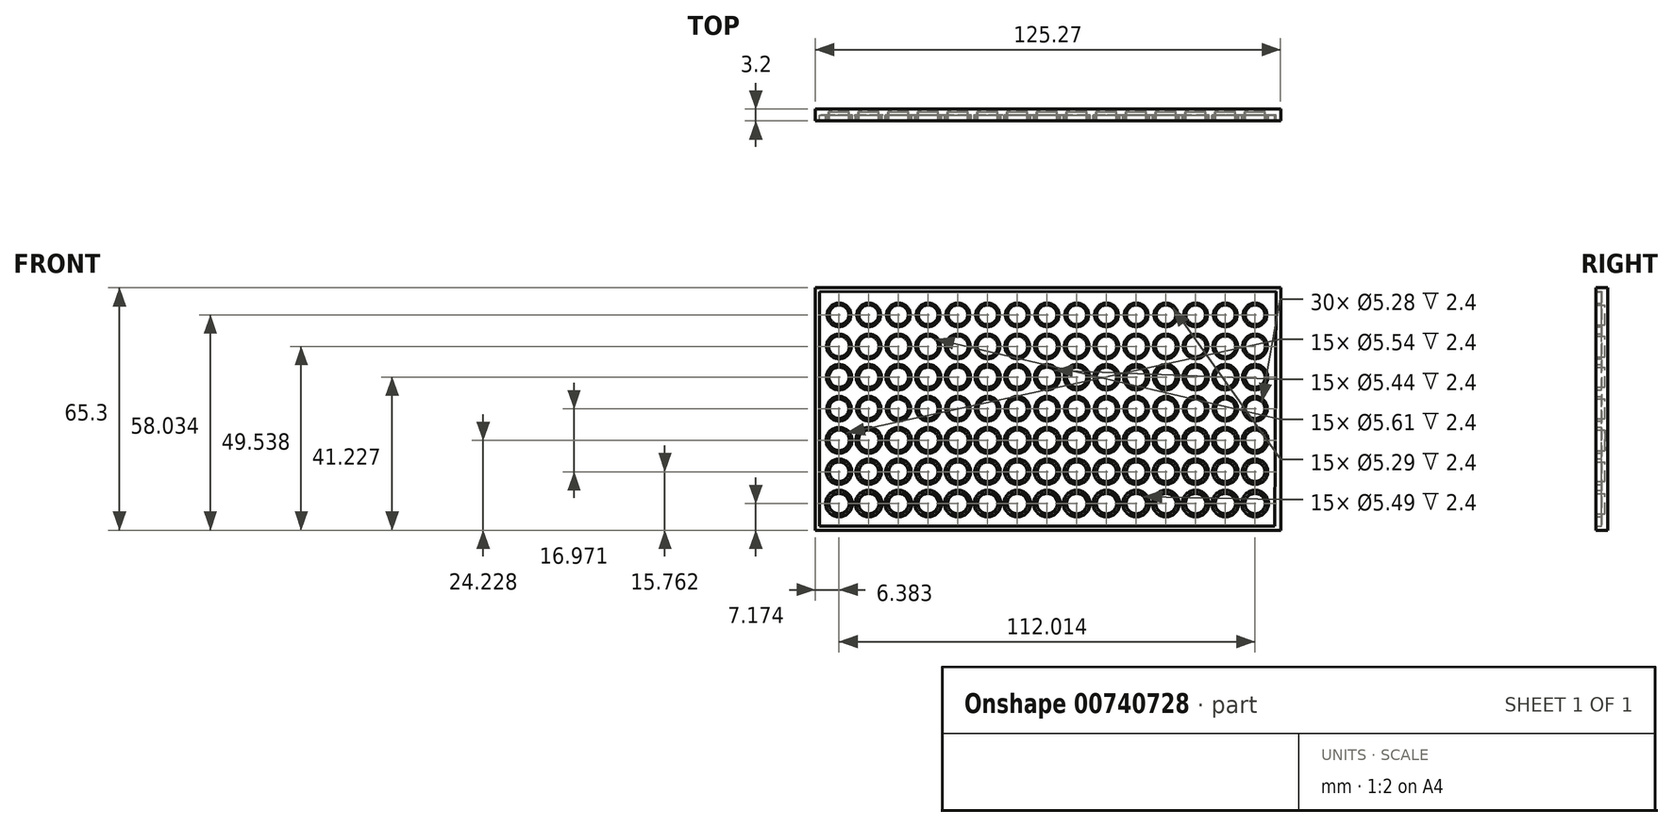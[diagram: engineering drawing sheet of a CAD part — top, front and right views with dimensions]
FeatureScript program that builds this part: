
annotation { "Feature Type Name" : "Feature", "Feature Type Description" : "" }
export const myFeature = defineFeature(function(context is Context, id is Id, definition is map)
    precondition{}
    {
        {
            var Q0;
            Q0=qCreatedBy(makeId("Front.planeOp"),FACE);
            var sketch = newSketch(context, id + "F0", { "sketchPlane" : qUnion([Q0])});
            skLineSegment(sketch, "E0", {"start": v(-62.27, 44.26) * mm, "end": v(-62.27, -21.04) * mm});
            skLineSegment(sketch, "E1", {"start": v(-62.27, -21.04) * mm, "end": v(63, -21.04) * mm});
            skLineSegment(sketch, "E2", {"start": v(63, -21.04) * mm, "end": v(63, 44.26) * mm});
            skLineSegment(sketch, "E3", {"start": v(63, 44.26) * mm, "end": v(-62.27, 44.26) * mm});
            skLineSegment(sketch, "E4", {"start": v(-61.12, 43.24) * mm, "end": v(-61.12, -19.95) * mm});
            skLineSegment(sketch, "E5", {"start": v(-61.12, -19.95) * mm, "end": v(61.46, -19.95) * mm});
            skLineSegment(sketch, "E6", {"start": v(61.46, -19.95) * mm, "end": v(61.83, 43.36) * mm});
            skLineSegment(sketch, "E7", {"start": v(61.83, 43.36) * mm, "end": v(-61.12, 43.24) * mm});
            skCircle(sketch, "E8", {"center": v(-55.89, 28.5) * mm, "radius": 2.8 * mm});
            skCircle(sketch, "E9", {"center": v(-55.89, 28.5) * mm, "radius": 3.32 * mm});
            skCircle(sketch, "E10.1.0.0", {"center": v(-47.89, 28.5) * mm, "radius": 3.32 * mm});
            skCircle(sketch, "E10.1.0.1", {"center": v(-47.89, 28.5) * mm, "radius": 2.8 * mm});
            skCircle(sketch, "E10.2.0.0", {"center": v(-39.89, 28.5) * mm, "radius": 3.32 * mm});
            skCircle(sketch, "E10.2.0.1", {"center": v(-39.89, 28.5) * mm, "radius": 2.8 * mm});
            skCircle(sketch, "E10.3.0.0", {"center": v(-31.88, 28.5) * mm, "radius": 3.32 * mm});
            skCircle(sketch, "E10.3.0.1", {"center": v(-31.88, 28.5) * mm, "radius": 2.8 * mm});
            skCircle(sketch, "E10.4.0.0", {"center": v(-23.88, 28.5) * mm, "radius": 3.32 * mm});
            skCircle(sketch, "E10.4.0.1", {"center": v(-23.88, 28.5) * mm, "radius": 2.8 * mm});
            skCircle(sketch, "E10.5.0.0", {"center": v(-15.88, 28.5) * mm, "radius": 3.32 * mm});
            skCircle(sketch, "E10.5.0.1", {"center": v(-15.88, 28.5) * mm, "radius": 2.8 * mm});
            skCircle(sketch, "E10.6.0.0", {"center": v(-7.88, 28.5) * mm, "radius": 3.32 * mm});
            skCircle(sketch, "E10.6.0.1", {"center": v(-7.88, 28.5) * mm, "radius": 2.8 * mm});
            skCircle(sketch, "E10.7.0.0", {"center": v(0.12, 28.5) * mm, "radius": 3.32 * mm});
            skCircle(sketch, "E10.7.0.1", {"center": v(0.12, 28.5) * mm, "radius": 2.8 * mm});
            skCircle(sketch, "E10.8.0.0", {"center": v(8.12, 28.5) * mm, "radius": 3.32 * mm});
            skCircle(sketch, "E10.8.0.1", {"center": v(8.12, 28.5) * mm, "radius": 2.8 * mm});
            skCircle(sketch, "E10.9.0.0", {"center": v(16.12, 28.5) * mm, "radius": 3.32 * mm});
            skCircle(sketch, "E10.9.0.1", {"center": v(16.12, 28.5) * mm, "radius": 2.8 * mm});
            skCircle(sketch, "E10.10.0.0", {"center": v(24.12, 28.5) * mm, "radius": 3.32 * mm});
            skCircle(sketch, "E10.10.0.1", {"center": v(24.12, 28.5) * mm, "radius": 2.8 * mm});
            skCircle(sketch, "E10.11.0.0", {"center": v(32.12, 28.5) * mm, "radius": 3.32 * mm});
            skCircle(sketch, "E10.11.0.1", {"center": v(32.12, 28.5) * mm, "radius": 2.8 * mm});
            skCircle(sketch, "E10.12.0.0", {"center": v(40.12, 28.5) * mm, "radius": 3.32 * mm});
            skCircle(sketch, "E10.12.0.1", {"center": v(40.12, 28.5) * mm, "radius": 2.8 * mm});
            skCircle(sketch, "E10.13.0.0", {"center": v(48.13, 28.5) * mm, "radius": 3.32 * mm});
            skCircle(sketch, "E10.13.0.1", {"center": v(48.13, 28.5) * mm, "radius": 2.8 * mm});
            skCircle(sketch, "E10.14.0.0", {"center": v(56.13, 28.5) * mm, "radius": 3.32 * mm});
            skCircle(sketch, "E10.14.0.1", {"center": v(56.13, 28.5) * mm, "radius": 2.8 * mm});
            skLineSegment(sketch, "E10.direction1", {"start": v(-55.89, 28.5) * mm, "end": v(-47.89, 28.5) * mm, "construction": true});
            skCircle(sketch, "E11", {"center": v(-55.89, 37) * mm, "radius": 2.65 * mm});
            skCircle(sketch, "E12", {"center": v(-55.89, 37) * mm, "radius": 3.2 * mm});
            skCircle(sketch, "E13.1.0.0", {"center": v(-47.89, 37) * mm, "radius": 3.2 * mm});
            skCircle(sketch, "E13.1.0.1", {"center": v(-47.89, 37) * mm, "radius": 2.65 * mm});
            skCircle(sketch, "E13.2.0.0", {"center": v(-39.89, 37) * mm, "radius": 3.2 * mm});
            skCircle(sketch, "E13.2.0.1", {"center": v(-39.89, 37) * mm, "radius": 2.65 * mm});
            skCircle(sketch, "E13.3.0.0", {"center": v(-31.88, 37) * mm, "radius": 3.2 * mm});
            skCircle(sketch, "E13.3.0.1", {"center": v(-31.88, 37) * mm, "radius": 2.65 * mm});
            skCircle(sketch, "E13.4.0.0", {"center": v(-23.88, 37) * mm, "radius": 3.2 * mm});
            skCircle(sketch, "E13.4.0.1", {"center": v(-23.88, 37) * mm, "radius": 2.65 * mm});
            skCircle(sketch, "E13.5.0.0", {"center": v(-15.88, 37) * mm, "radius": 3.2 * mm});
            skCircle(sketch, "E13.5.0.1", {"center": v(-15.88, 37) * mm, "radius": 2.65 * mm});
            skCircle(sketch, "E13.6.0.0", {"center": v(-7.88, 37) * mm, "radius": 3.2 * mm});
            skCircle(sketch, "E13.6.0.1", {"center": v(-7.88, 37) * mm, "radius": 2.65 * mm});
            skCircle(sketch, "E13.7.0.0", {"center": v(0.12, 37) * mm, "radius": 3.2 * mm});
            skCircle(sketch, "E13.7.0.1", {"center": v(0.12, 37) * mm, "radius": 2.65 * mm});
            skCircle(sketch, "E13.8.0.0", {"center": v(8.12, 37) * mm, "radius": 3.2 * mm});
            skCircle(sketch, "E13.8.0.1", {"center": v(8.12, 37) * mm, "radius": 2.65 * mm});
            skCircle(sketch, "E13.9.0.0", {"center": v(16.12, 37) * mm, "radius": 3.2 * mm});
            skCircle(sketch, "E13.9.0.1", {"center": v(16.12, 37) * mm, "radius": 2.65 * mm});
            skCircle(sketch, "E13.10.0.0", {"center": v(24.12, 37) * mm, "radius": 3.2 * mm});
            skCircle(sketch, "E13.10.0.1", {"center": v(24.12, 37) * mm, "radius": 2.65 * mm});
            skCircle(sketch, "E13.11.0.0", {"center": v(32.12, 37) * mm, "radius": 3.2 * mm});
            skCircle(sketch, "E13.11.0.1", {"center": v(32.12, 37) * mm, "radius": 2.65 * mm});
            skCircle(sketch, "E13.12.0.0", {"center": v(40.12, 37) * mm, "radius": 3.2 * mm});
            skCircle(sketch, "E13.12.0.1", {"center": v(40.12, 37) * mm, "radius": 2.65 * mm});
            skCircle(sketch, "E13.13.0.0", {"center": v(48.13, 37) * mm, "radius": 3.2 * mm});
            skCircle(sketch, "E13.13.0.1", {"center": v(48.13, 37) * mm, "radius": 2.65 * mm});
            skCircle(sketch, "E13.14.0.0", {"center": v(56.13, 37) * mm, "radius": 3.2 * mm});
            skCircle(sketch, "E13.14.0.1", {"center": v(56.13, 37) * mm, "radius": 2.65 * mm});
            skLineSegment(sketch, "E13.direction1", {"start": v(-55.89, 37) * mm, "end": v(-47.89, 37) * mm, "construction": true});
            skCircle(sketch, "E14", {"center": v(-55.89, 20.19) * mm, "radius": 2.72 * mm});
            skCircle(sketch, "E15", {"center": v(-55.89, 20.19) * mm, "radius": 3.4 * mm});
            skCircle(sketch, "E16.1.0.0", {"center": v(-47.89, 20.19) * mm, "radius": 2.72 * mm});
            skCircle(sketch, "E16.1.0.1", {"center": v(-47.89, 20.19) * mm, "radius": 3.4 * mm});
            skCircle(sketch, "E16.2.0.0", {"center": v(-39.89, 20.19) * mm, "radius": 2.72 * mm});
            skCircle(sketch, "E16.2.0.1", {"center": v(-39.89, 20.19) * mm, "radius": 3.4 * mm});
            skCircle(sketch, "E16.3.0.0", {"center": v(-31.88, 20.19) * mm, "radius": 2.72 * mm});
            skCircle(sketch, "E16.3.0.1", {"center": v(-31.88, 20.19) * mm, "radius": 3.4 * mm});
            skCircle(sketch, "E16.4.0.0", {"center": v(-23.88, 20.19) * mm, "radius": 2.72 * mm});
            skCircle(sketch, "E16.4.0.1", {"center": v(-23.88, 20.19) * mm, "radius": 3.4 * mm});
            skCircle(sketch, "E16.5.0.0", {"center": v(-15.88, 20.19) * mm, "radius": 2.72 * mm});
            skCircle(sketch, "E16.5.0.1", {"center": v(-15.88, 20.19) * mm, "radius": 3.4 * mm});
            skCircle(sketch, "E16.6.0.0", {"center": v(-7.88, 20.19) * mm, "radius": 2.72 * mm});
            skCircle(sketch, "E16.6.0.1", {"center": v(-7.88, 20.19) * mm, "radius": 3.4 * mm});
            skCircle(sketch, "E16.7.0.0", {"center": v(0.12, 20.19) * mm, "radius": 2.72 * mm});
            skCircle(sketch, "E16.7.0.1", {"center": v(0.12, 20.19) * mm, "radius": 3.4 * mm});
            skCircle(sketch, "E16.8.0.0", {"center": v(8.12, 20.19) * mm, "radius": 2.72 * mm});
            skCircle(sketch, "E16.8.0.1", {"center": v(8.12, 20.19) * mm, "radius": 3.4 * mm});
            skCircle(sketch, "E16.9.0.0", {"center": v(16.12, 20.19) * mm, "radius": 2.72 * mm});
            skCircle(sketch, "E16.9.0.1", {"center": v(16.12, 20.19) * mm, "radius": 3.4 * mm});
            skCircle(sketch, "E16.10.0.0", {"center": v(24.12, 20.19) * mm, "radius": 2.72 * mm});
            skCircle(sketch, "E16.10.0.1", {"center": v(24.12, 20.19) * mm, "radius": 3.4 * mm});
            skCircle(sketch, "E16.11.0.0", {"center": v(32.12, 20.19) * mm, "radius": 2.72 * mm});
            skCircle(sketch, "E16.11.0.1", {"center": v(32.12, 20.19) * mm, "radius": 3.4 * mm});
            skCircle(sketch, "E16.12.0.0", {"center": v(40.12, 20.19) * mm, "radius": 2.72 * mm});
            skCircle(sketch, "E16.12.0.1", {"center": v(40.12, 20.19) * mm, "radius": 3.4 * mm});
            skCircle(sketch, "E16.13.0.0", {"center": v(48.13, 20.19) * mm, "radius": 2.72 * mm});
            skCircle(sketch, "E16.13.0.1", {"center": v(48.13, 20.19) * mm, "radius": 3.4 * mm});
            skCircle(sketch, "E16.14.0.0", {"center": v(56.13, 20.19) * mm, "radius": 2.72 * mm});
            skCircle(sketch, "E16.14.0.1", {"center": v(56.13, 20.19) * mm, "radius": 3.4 * mm});
            skLineSegment(sketch, "E16.direction1", {"start": v(-55.89, 20.19) * mm, "end": v(-47.89, 20.19) * mm, "construction": true});
            skCircle(sketch, "E17", {"center": v(-55.89, 11.7) * mm, "radius": 2.64 * mm});
            skCircle(sketch, "E18", {"center": v(-55.89, 11.7) * mm, "radius": 3.3 * mm});
            skCircle(sketch, "E19.1.0.0", {"center": v(-47.89, 11.7) * mm, "radius": 2.64 * mm});
            skCircle(sketch, "E19.1.0.1", {"center": v(-47.89, 11.7) * mm, "radius": 3.3 * mm});
            skCircle(sketch, "E19.2.0.0", {"center": v(-39.89, 11.7) * mm, "radius": 2.64 * mm});
            skCircle(sketch, "E19.2.0.1", {"center": v(-39.89, 11.7) * mm, "radius": 3.3 * mm});
            skCircle(sketch, "E19.3.0.0", {"center": v(-31.88, 11.7) * mm, "radius": 2.64 * mm});
            skCircle(sketch, "E19.3.0.1", {"center": v(-31.88, 11.7) * mm, "radius": 3.3 * mm});
            skCircle(sketch, "E19.4.0.0", {"center": v(-23.88, 11.7) * mm, "radius": 2.64 * mm});
            skCircle(sketch, "E19.4.0.1", {"center": v(-23.88, 11.7) * mm, "radius": 3.3 * mm});
            skCircle(sketch, "E19.5.0.0", {"center": v(-15.88, 11.7) * mm, "radius": 2.64 * mm});
            skCircle(sketch, "E19.5.0.1", {"center": v(-15.88, 11.7) * mm, "radius": 3.3 * mm});
            skCircle(sketch, "E19.6.0.0", {"center": v(-7.88, 11.7) * mm, "radius": 2.64 * mm});
            skCircle(sketch, "E19.6.0.1", {"center": v(-7.88, 11.7) * mm, "radius": 3.3 * mm});
            skCircle(sketch, "E19.7.0.0", {"center": v(0.12, 11.7) * mm, "radius": 2.64 * mm});
            skCircle(sketch, "E19.7.0.1", {"center": v(0.12, 11.7) * mm, "radius": 3.3 * mm});
            skCircle(sketch, "E19.8.0.0", {"center": v(8.12, 11.7) * mm, "radius": 2.64 * mm});
            skCircle(sketch, "E19.8.0.1", {"center": v(8.12, 11.7) * mm, "radius": 3.3 * mm});
            skCircle(sketch, "E19.9.0.0", {"center": v(16.12, 11.7) * mm, "radius": 2.64 * mm});
            skCircle(sketch, "E19.9.0.1", {"center": v(16.12, 11.7) * mm, "radius": 3.3 * mm});
            skCircle(sketch, "E19.10.0.0", {"center": v(24.12, 11.7) * mm, "radius": 2.64 * mm});
            skCircle(sketch, "E19.10.0.1", {"center": v(24.12, 11.7) * mm, "radius": 3.3 * mm});
            skCircle(sketch, "E19.11.0.0", {"center": v(32.12, 11.7) * mm, "radius": 2.64 * mm});
            skCircle(sketch, "E19.11.0.1", {"center": v(32.12, 11.7) * mm, "radius": 3.3 * mm});
            skCircle(sketch, "E19.12.0.0", {"center": v(40.12, 11.7) * mm, "radius": 2.64 * mm});
            skCircle(sketch, "E19.12.0.1", {"center": v(40.12, 11.7) * mm, "radius": 3.3 * mm});
            skCircle(sketch, "E19.13.0.0", {"center": v(48.13, 11.7) * mm, "radius": 2.64 * mm});
            skCircle(sketch, "E19.13.0.1", {"center": v(48.13, 11.7) * mm, "radius": 3.3 * mm});
            skCircle(sketch, "E19.14.0.0", {"center": v(56.13, 11.7) * mm, "radius": 2.64 * mm});
            skCircle(sketch, "E19.14.0.1", {"center": v(56.13, 11.7) * mm, "radius": 3.3 * mm});
            skLineSegment(sketch, "E19.direction1", {"start": v(-55.89, 11.7) * mm, "end": v(-47.89, 11.7) * mm, "construction": true});
            skCircle(sketch, "E20", {"center": v(-55.89, 3.19) * mm, "radius": 2.77 * mm});
            skCircle(sketch, "E21", {"center": v(-55.89, 3.19) * mm, "radius": 3.48 * mm});
            skCircle(sketch, "E22.1.0.0", {"center": v(-47.89, 3.19) * mm, "radius": 2.77 * mm});
            skCircle(sketch, "E22.1.0.1", {"center": v(-47.89, 3.19) * mm, "radius": 3.48 * mm});
            skCircle(sketch, "E22.2.0.0", {"center": v(-39.89, 3.19) * mm, "radius": 2.77 * mm});
            skCircle(sketch, "E22.2.0.1", {"center": v(-39.89, 3.19) * mm, "radius": 3.48 * mm});
            skCircle(sketch, "E22.3.0.0", {"center": v(-31.88, 3.19) * mm, "radius": 2.77 * mm});
            skCircle(sketch, "E22.3.0.1", {"center": v(-31.88, 3.19) * mm, "radius": 3.48 * mm});
            skCircle(sketch, "E22.4.0.0", {"center": v(-23.88, 3.19) * mm, "radius": 2.77 * mm});
            skCircle(sketch, "E22.4.0.1", {"center": v(-23.88, 3.19) * mm, "radius": 3.48 * mm});
            skCircle(sketch, "E22.5.0.0", {"center": v(-15.88, 3.19) * mm, "radius": 2.77 * mm});
            skCircle(sketch, "E22.5.0.1", {"center": v(-15.88, 3.19) * mm, "radius": 3.48 * mm});
            skCircle(sketch, "E22.6.0.0", {"center": v(-7.88, 3.19) * mm, "radius": 2.77 * mm});
            skCircle(sketch, "E22.6.0.1", {"center": v(-7.88, 3.19) * mm, "radius": 3.48 * mm});
            skCircle(sketch, "E22.7.0.0", {"center": v(0.12, 3.19) * mm, "radius": 2.77 * mm});
            skCircle(sketch, "E22.7.0.1", {"center": v(0.12, 3.19) * mm, "radius": 3.48 * mm});
            skCircle(sketch, "E22.8.0.0", {"center": v(8.12, 3.19) * mm, "radius": 2.77 * mm});
            skCircle(sketch, "E22.8.0.1", {"center": v(8.12, 3.19) * mm, "radius": 3.48 * mm});
            skCircle(sketch, "E22.9.0.0", {"center": v(16.12, 3.19) * mm, "radius": 2.77 * mm});
            skCircle(sketch, "E22.9.0.1", {"center": v(16.12, 3.19) * mm, "radius": 3.48 * mm});
            skCircle(sketch, "E22.10.0.0", {"center": v(24.12, 3.19) * mm, "radius": 2.77 * mm});
            skCircle(sketch, "E22.10.0.1", {"center": v(24.12, 3.19) * mm, "radius": 3.48 * mm});
            skCircle(sketch, "E22.11.0.0", {"center": v(32.12, 3.19) * mm, "radius": 2.77 * mm});
            skCircle(sketch, "E22.11.0.1", {"center": v(32.12, 3.19) * mm, "radius": 3.48 * mm});
            skCircle(sketch, "E22.12.0.0", {"center": v(40.12, 3.19) * mm, "radius": 2.77 * mm});
            skCircle(sketch, "E22.12.0.1", {"center": v(40.12, 3.19) * mm, "radius": 3.48 * mm});
            skCircle(sketch, "E22.13.0.0", {"center": v(48.13, 3.19) * mm, "radius": 2.77 * mm});
            skCircle(sketch, "E22.13.0.1", {"center": v(48.13, 3.19) * mm, "radius": 3.48 * mm});
            skCircle(sketch, "E22.14.0.0", {"center": v(56.13, 3.19) * mm, "radius": 2.77 * mm});
            skCircle(sketch, "E22.14.0.1", {"center": v(56.13, 3.19) * mm, "radius": 3.48 * mm});
            skLineSegment(sketch, "E22.direction1", {"start": v(-55.89, 3.19) * mm, "end": v(-47.89, 3.19) * mm, "construction": true});
            skCircle(sketch, "E23", {"center": v(-55.89, -5.28) * mm, "radius": 2.64 * mm});
            skCircle(sketch, "E24", {"center": v(-55.89, -5.28) * mm, "radius": 3.44 * mm});
            skCircle(sketch, "E25", {"center": v(-55.89, -13.87) * mm, "radius": 2.74 * mm});
            skCircle(sketch, "E26", {"center": v(-55.89, -13.87) * mm, "radius": 3.6 * mm});
            skCircle(sketch, "E27.1.0.0", {"center": v(-47.89, -5.28) * mm, "radius": 2.64 * mm});
            skCircle(sketch, "E27.1.0.1", {"center": v(-47.89, -5.28) * mm, "radius": 3.44 * mm});
            skCircle(sketch, "E27.2.0.0", {"center": v(-39.89, -5.28) * mm, "radius": 2.64 * mm});
            skCircle(sketch, "E27.2.0.1", {"center": v(-39.89, -5.28) * mm, "radius": 3.44 * mm});
            skCircle(sketch, "E27.3.0.0", {"center": v(-31.88, -5.28) * mm, "radius": 2.64 * mm});
            skCircle(sketch, "E27.3.0.1", {"center": v(-31.88, -5.28) * mm, "radius": 3.44 * mm});
            skCircle(sketch, "E27.4.0.0", {"center": v(-23.88, -5.28) * mm, "radius": 2.64 * mm});
            skCircle(sketch, "E27.4.0.1", {"center": v(-23.88, -5.28) * mm, "radius": 3.44 * mm});
            skCircle(sketch, "E27.5.0.0", {"center": v(-15.88, -5.28) * mm, "radius": 2.64 * mm});
            skCircle(sketch, "E27.5.0.1", {"center": v(-15.88, -5.28) * mm, "radius": 3.44 * mm});
            skCircle(sketch, "E27.6.0.0", {"center": v(-7.88, -5.28) * mm, "radius": 2.64 * mm});
            skCircle(sketch, "E27.6.0.1", {"center": v(-7.88, -5.28) * mm, "radius": 3.44 * mm});
            skCircle(sketch, "E27.7.0.0", {"center": v(0.12, -5.28) * mm, "radius": 2.64 * mm});
            skCircle(sketch, "E27.7.0.1", {"center": v(0.12, -5.28) * mm, "radius": 3.44 * mm});
            skCircle(sketch, "E27.8.0.0", {"center": v(8.12, -5.28) * mm, "radius": 2.64 * mm});
            skCircle(sketch, "E27.8.0.1", {"center": v(8.12, -5.28) * mm, "radius": 3.44 * mm});
            skCircle(sketch, "E27.9.0.0", {"center": v(16.12, -5.28) * mm, "radius": 2.64 * mm});
            skCircle(sketch, "E27.9.0.1", {"center": v(16.12, -5.28) * mm, "radius": 3.44 * mm});
            skCircle(sketch, "E27.10.0.0", {"center": v(24.12, -5.28) * mm, "radius": 2.64 * mm});
            skCircle(sketch, "E27.10.0.1", {"center": v(24.12, -5.28) * mm, "radius": 3.44 * mm});
            skCircle(sketch, "E27.11.0.0", {"center": v(32.12, -5.28) * mm, "radius": 2.64 * mm});
            skCircle(sketch, "E27.11.0.1", {"center": v(32.12, -5.28) * mm, "radius": 3.44 * mm});
            skCircle(sketch, "E27.12.0.0", {"center": v(40.12, -5.28) * mm, "radius": 2.64 * mm});
            skCircle(sketch, "E27.12.0.1", {"center": v(40.12, -5.28) * mm, "radius": 3.44 * mm});
            skCircle(sketch, "E27.13.0.0", {"center": v(48.13, -5.28) * mm, "radius": 2.64 * mm});
            skCircle(sketch, "E27.13.0.1", {"center": v(48.13, -5.28) * mm, "radius": 3.44 * mm});
            skCircle(sketch, "E27.14.0.0", {"center": v(56.13, -5.28) * mm, "radius": 2.64 * mm});
            skCircle(sketch, "E27.14.0.1", {"center": v(56.13, -5.28) * mm, "radius": 3.44 * mm});
            skLineSegment(sketch, "E27.direction1", {"start": v(-55.89, -5.28) * mm, "end": v(-47.89, -5.28) * mm, "construction": true});
            skCircle(sketch, "E28.1.0.0", {"center": v(-47.89, -13.87) * mm, "radius": 2.74 * mm});
            skCircle(sketch, "E28.1.0.1", {"center": v(-47.89, -13.87) * mm, "radius": 3.6 * mm});
            skCircle(sketch, "E28.2.0.0", {"center": v(-39.89, -13.87) * mm, "radius": 2.74 * mm});
            skCircle(sketch, "E28.2.0.1", {"center": v(-39.89, -13.87) * mm, "radius": 3.6 * mm});
            skCircle(sketch, "E28.3.0.0", {"center": v(-31.88, -13.87) * mm, "radius": 2.74 * mm});
            skCircle(sketch, "E28.3.0.1", {"center": v(-31.88, -13.87) * mm, "radius": 3.6 * mm});
            skCircle(sketch, "E28.4.0.0", {"center": v(-23.88, -13.87) * mm, "radius": 2.74 * mm});
            skCircle(sketch, "E28.4.0.1", {"center": v(-23.88, -13.87) * mm, "radius": 3.6 * mm});
            skCircle(sketch, "E28.5.0.0", {"center": v(-15.88, -13.87) * mm, "radius": 2.74 * mm});
            skCircle(sketch, "E28.5.0.1", {"center": v(-15.88, -13.87) * mm, "radius": 3.6 * mm});
            skCircle(sketch, "E28.6.0.0", {"center": v(-7.88, -13.87) * mm, "radius": 2.74 * mm});
            skCircle(sketch, "E28.6.0.1", {"center": v(-7.88, -13.87) * mm, "radius": 3.6 * mm});
            skCircle(sketch, "E28.7.0.0", {"center": v(0.12, -13.87) * mm, "radius": 2.74 * mm});
            skCircle(sketch, "E28.7.0.1", {"center": v(0.12, -13.87) * mm, "radius": 3.6 * mm});
            skCircle(sketch, "E28.8.0.0", {"center": v(8.12, -13.87) * mm, "radius": 2.74 * mm});
            skCircle(sketch, "E28.8.0.1", {"center": v(8.12, -13.87) * mm, "radius": 3.6 * mm});
            skCircle(sketch, "E28.9.0.0", {"center": v(16.12, -13.87) * mm, "radius": 2.74 * mm});
            skCircle(sketch, "E28.9.0.1", {"center": v(16.12, -13.87) * mm, "radius": 3.6 * mm});
            skCircle(sketch, "E28.10.0.0", {"center": v(24.12, -13.87) * mm, "radius": 2.74 * mm});
            skCircle(sketch, "E28.10.0.1", {"center": v(24.12, -13.87) * mm, "radius": 3.6 * mm});
            skCircle(sketch, "E28.11.0.0", {"center": v(32.12, -13.87) * mm, "radius": 2.74 * mm});
            skCircle(sketch, "E28.11.0.1", {"center": v(32.12, -13.87) * mm, "radius": 3.6 * mm});
            skCircle(sketch, "E28.12.0.0", {"center": v(40.12, -13.87) * mm, "radius": 2.74 * mm});
            skCircle(sketch, "E28.12.0.1", {"center": v(40.12, -13.87) * mm, "radius": 3.6 * mm});
            skCircle(sketch, "E28.13.0.0", {"center": v(48.13, -13.87) * mm, "radius": 2.74 * mm});
            skCircle(sketch, "E28.13.0.1", {"center": v(48.13, -13.87) * mm, "radius": 3.6 * mm});
            skCircle(sketch, "E28.14.0.0", {"center": v(56.13, -13.87) * mm, "radius": 2.74 * mm});
            skCircle(sketch, "E28.14.0.1", {"center": v(56.13, -13.87) * mm, "radius": 3.6 * mm});
            skLineSegment(sketch, "E28.direction1", {"start": v(-55.89, -13.87) * mm, "end": v(-47.89, -13.87) * mm, "construction": true});
            skSolve(sketch);
        }
        {
            var Q0;
            Q0=makeQuery(id+"F0.imprint","IMPRINT",FACE,{"disambiguationData":[TD([[makeQuery(id+"F0.imprint","IMPRINT",EDGE,{"derivedFrom":sQuery(id+"F0.wireOp",EDGE,"E0")}),1.0]])]});
            extrude(context, id + "F1", {"entities" : qUnion([Q0]), "depth" : 3.2 * mm, "offsetDistance" : 25.4 * mm});
        }
        {
            var Q0;
            Q0=makeQuery(id+"F0.imprint","IMPRINT",FACE,{"disambiguationData":[TD([[makeQuery(id+"F0.imprint","IMPRINT",EDGE,{"derivedFrom":sQuery(id+"F0.wireOp",EDGE,"E4")}),1.0]])]});
            extrude(context, id + "F2", {"entities" : qUnion([Q0]), "operationType" : NewBodyOperationType.ADD, "depth" : 1.7 * mm, "offsetDistance" : 25.4 * mm});
        }
        {
            var Q0;
            Q0 = qSketchRegion(id + "F0", true);
            var Q1;
            Q1=makeQuery(id+"F0.imprint","IMPRINT",FACE,{"disambiguationData":[TD([[makeQuery(id+"F0.imprint","IMPRINT",EDGE,{"derivedFrom":sQuery(id+"F0.wireOp",EDGE,"E23")}),-1.0]])]});
            var Q2;
            Q2=makeQuery(id+"F0.imprint","IMPRINT",FACE,{"disambiguationData":[TD([[makeQuery(id+"F0.imprint","IMPRINT",EDGE,{"derivedFrom":sQuery(id+"F0.wireOp",EDGE,"E25")}),-1.0]])]});
            var Q3;
            Q3=makeQuery(id+"F0.imprint","IMPRINT",FACE,{"disambiguationData":[TD([[makeQuery(id+"F0.imprint","IMPRINT",EDGE,{"derivedFrom":sQuery(id+"F0.wireOp",EDGE,"E27.1.0.0")}),-1.0]])]});
            var Q4;
            Q4=makeQuery(id+"F0.imprint","IMPRINT",FACE,{"disambiguationData":[TD([[makeQuery(id+"F0.imprint","IMPRINT",EDGE,{"derivedFrom":sQuery(id+"F0.wireOp",EDGE,"E22.1.0.0")}),-1.0]])]});
            var Q5;
            Q5=makeQuery(id+"F0.imprint","IMPRINT",FACE,{"disambiguationData":[TD([[makeQuery(id+"F0.imprint","IMPRINT",EDGE,{"derivedFrom":sQuery(id+"F0.wireOp",EDGE,"E20")}),-1.0]])]});
            var Q6;
            Q6=makeQuery(id+"F0.imprint","IMPRINT",FACE,{"disambiguationData":[TD([[makeQuery(id+"F0.imprint","IMPRINT",EDGE,{"derivedFrom":sQuery(id+"F0.wireOp",EDGE,"E28.1.0.0")}),-1.0]])]});
            var Q7;
            Q7=makeQuery(id+"F0.imprint","IMPRINT",FACE,{"disambiguationData":[TD([[makeQuery(id+"F0.imprint","IMPRINT",EDGE,{"derivedFrom":sQuery(id+"F0.wireOp",EDGE,"E28.2.0.0")}),-1.0]])]});
            var Q8;
            Q8=makeQuery(id+"F0.imprint","IMPRINT",FACE,{"disambiguationData":[TD([[makeQuery(id+"F0.imprint","IMPRINT",EDGE,{"derivedFrom":sQuery(id+"F0.wireOp",EDGE,"E27.2.0.0")}),-1.0]])]});
            var Q9;
            Q9=makeQuery(id+"F0.imprint","IMPRINT",FACE,{"disambiguationData":[TD([[makeQuery(id+"F0.imprint","IMPRINT",EDGE,{"derivedFrom":sQuery(id+"F0.wireOp",EDGE,"E22.2.0.0")}),-1.0]])]});
            var Q10;
            Q10=makeQuery(id+"F0.imprint","IMPRINT",FACE,{"disambiguationData":[TD([[makeQuery(id+"F0.imprint","IMPRINT",EDGE,{"derivedFrom":sQuery(id+"F0.wireOp",EDGE,"E19.2.0.0")}),-1.0]])]});
            var Q11;
            Q11=makeQuery(id+"F0.imprint","IMPRINT",FACE,{"disambiguationData":[TD([[makeQuery(id+"F0.imprint","IMPRINT",EDGE,{"derivedFrom":sQuery(id+"F0.wireOp",EDGE,"E19.1.0.0")}),-1.0]])]});
            var Q12;
            Q12=makeQuery(id+"F0.imprint","IMPRINT",FACE,{"disambiguationData":[TD([[makeQuery(id+"F0.imprint","IMPRINT",EDGE,{"derivedFrom":sQuery(id+"F0.wireOp",EDGE,"E17")}),-1.0]])]});
            var Q13;
            Q13=makeQuery(id+"F0.imprint","IMPRINT",FACE,{"disambiguationData":[TD([[makeQuery(id+"F0.imprint","IMPRINT",EDGE,{"derivedFrom":sQuery(id+"F0.wireOp",EDGE,"E14")}),-1.0]])]});
            var Q14;
            Q14=makeQuery(id+"F0.imprint","IMPRINT",FACE,{"disambiguationData":[TD([[makeQuery(id+"F0.imprint","IMPRINT",EDGE,{"derivedFrom":sQuery(id+"F0.wireOp",EDGE,"E16.1.0.0")}),-1.0]])]});
            var Q15;
            Q15=makeQuery(id+"F0.imprint","IMPRINT",FACE,{"disambiguationData":[TD([[makeQuery(id+"F0.imprint","IMPRINT",EDGE,{"derivedFrom":sQuery(id+"F0.wireOp",EDGE,"E10.1.0.0")}),1.0]])]});
            var Q16;
            Q16=makeQuery(id+"F0.imprint","IMPRINT",FACE,{"disambiguationData":[TD([[makeQuery(id+"F0.imprint","IMPRINT",EDGE,{"derivedFrom":sQuery(id+"F0.wireOp",EDGE,"E8")}),-1.0]])]});
            var Q17;
            Q17=makeQuery(id+"F0.imprint","IMPRINT",FACE,{"disambiguationData":[TD([[makeQuery(id+"F0.imprint","IMPRINT",EDGE,{"derivedFrom":sQuery(id+"F0.wireOp",EDGE,"E16.2.0.0")}),-1.0]])]});
            var Q18;
            Q18=makeQuery(id+"F0.imprint","IMPRINT",FACE,{"disambiguationData":[TD([[makeQuery(id+"F0.imprint","IMPRINT",EDGE,{"derivedFrom":sQuery(id+"F0.wireOp",EDGE,"E10.2.0.0")}),1.0]])]});
            var Q19;
            Q19=makeQuery(id+"F0.imprint","IMPRINT",FACE,{"disambiguationData":[TD([[makeQuery(id+"F0.imprint","IMPRINT",EDGE,{"derivedFrom":sQuery(id+"F0.wireOp",EDGE,"E16.3.0.0")}),-1.0]])]});
            var Q20;
            Q20=makeQuery(id+"F0.imprint","IMPRINT",FACE,{"disambiguationData":[TD([[makeQuery(id+"F0.imprint","IMPRINT",EDGE,{"derivedFrom":sQuery(id+"F0.wireOp",EDGE,"E19.3.0.0")}),-1.0]])]});
            var Q21;
            Q21=makeQuery(id+"F0.imprint","IMPRINT",FACE,{"disambiguationData":[TD([[makeQuery(id+"F0.imprint","IMPRINT",EDGE,{"derivedFrom":sQuery(id+"F0.wireOp",EDGE,"E11")}),-1.0]])]});
            var Q22;
            Q22=makeQuery(id+"F0.imprint","IMPRINT",FACE,{"disambiguationData":[TD([[makeQuery(id+"F0.imprint","IMPRINT",EDGE,{"derivedFrom":sQuery(id+"F0.wireOp",EDGE,"E13.1.0.0")}),1.0]])]});
            var Q23;
            Q23=makeQuery(id+"F0.imprint","IMPRINT",FACE,{"disambiguationData":[TD([[makeQuery(id+"F0.imprint","IMPRINT",EDGE,{"derivedFrom":sQuery(id+"F0.wireOp",EDGE,"E13.2.0.0")}),1.0]])]});
            var Q24;
            Q24=makeQuery(id+"F0.imprint","IMPRINT",FACE,{"disambiguationData":[TD([[makeQuery(id+"F0.imprint","IMPRINT",EDGE,{"derivedFrom":sQuery(id+"F0.wireOp",EDGE,"E10.3.0.0")}),1.0]])]});
            var Q25;
            Q25=makeQuery(id+"F0.imprint","IMPRINT",FACE,{"disambiguationData":[TD([[makeQuery(id+"F0.imprint","IMPRINT",EDGE,{"derivedFrom":sQuery(id+"F0.wireOp",EDGE,"E28.3.0.0")}),-1.0]])]});
            var Q26;
            Q26=makeQuery(id+"F0.imprint","IMPRINT",FACE,{"disambiguationData":[TD([[makeQuery(id+"F0.imprint","IMPRINT",EDGE,{"derivedFrom":sQuery(id+"F0.wireOp",EDGE,"E28.4.0.0")}),-1.0]])]});
            var Q27;
            Q27=makeQuery(id+"F0.imprint","IMPRINT",FACE,{"disambiguationData":[TD([[makeQuery(id+"F0.imprint","IMPRINT",EDGE,{"derivedFrom":sQuery(id+"F0.wireOp",EDGE,"E27.4.0.0")}),-1.0]])]});
            var Q28;
            Q28=makeQuery(id+"F0.imprint","IMPRINT",FACE,{"disambiguationData":[TD([[makeQuery(id+"F0.imprint","IMPRINT",EDGE,{"derivedFrom":sQuery(id+"F0.wireOp",EDGE,"E27.3.0.0")}),-1.0]])]});
            var Q29;
            Q29=makeQuery(id+"F0.imprint","IMPRINT",FACE,{"disambiguationData":[TD([[makeQuery(id+"F0.imprint","IMPRINT",EDGE,{"derivedFrom":sQuery(id+"F0.wireOp",EDGE,"E22.3.0.0")}),-1.0]])]});
            var Q30;
            Q30=makeQuery(id+"F0.imprint","IMPRINT",FACE,{"disambiguationData":[TD([[makeQuery(id+"F0.imprint","IMPRINT",EDGE,{"derivedFrom":sQuery(id+"F0.wireOp",EDGE,"E22.4.0.0")}),-1.0]])]});
            var Q31;
            Q31=makeQuery(id+"F0.imprint","IMPRINT",FACE,{"disambiguationData":[TD([[makeQuery(id+"F0.imprint","IMPRINT",EDGE,{"derivedFrom":sQuery(id+"F0.wireOp",EDGE,"E19.4.0.0")}),-1.0]])]});
            var Q32;
            Q32=makeQuery(id+"F0.imprint","IMPRINT",FACE,{"disambiguationData":[TD([[makeQuery(id+"F0.imprint","IMPRINT",EDGE,{"derivedFrom":sQuery(id+"F0.wireOp",EDGE,"E16.4.0.0")}),-1.0]])]});
            var Q33;
            Q33=makeQuery(id+"F0.imprint","IMPRINT",FACE,{"disambiguationData":[TD([[makeQuery(id+"F0.imprint","IMPRINT",EDGE,{"derivedFrom":sQuery(id+"F0.wireOp",EDGE,"E10.4.0.0")}),1.0]])]});
            var Q34;
            Q34=makeQuery(id+"F0.imprint","IMPRINT",FACE,{"disambiguationData":[TD([[makeQuery(id+"F0.imprint","IMPRINT",EDGE,{"derivedFrom":sQuery(id+"F0.wireOp",EDGE,"E13.4.0.0")}),1.0]])]});
            var Q35;
            Q35=makeQuery(id+"F0.imprint","IMPRINT",FACE,{"disambiguationData":[TD([[makeQuery(id+"F0.imprint","IMPRINT",EDGE,{"derivedFrom":sQuery(id+"F0.wireOp",EDGE,"E13.3.0.0")}),1.0]])]});
            var Q36;
            Q36=makeQuery(id+"F0.imprint","IMPRINT",FACE,{"disambiguationData":[TD([[makeQuery(id+"F0.imprint","IMPRINT",EDGE,{"derivedFrom":sQuery(id+"F0.wireOp",EDGE,"E13.5.0.0")}),1.0]])]});
            var Q37;
            Q37=makeQuery(id+"F0.imprint","IMPRINT",FACE,{"disambiguationData":[TD([[makeQuery(id+"F0.imprint","IMPRINT",EDGE,{"derivedFrom":sQuery(id+"F0.wireOp",EDGE,"E13.6.0.0")}),1.0]])]});
            var Q38;
            Q38=makeQuery(id+"F0.imprint","IMPRINT",FACE,{"disambiguationData":[TD([[makeQuery(id+"F0.imprint","IMPRINT",EDGE,{"derivedFrom":sQuery(id+"F0.wireOp",EDGE,"E13.7.0.0")}),1.0]])]});
            var Q39;
            Q39=makeQuery(id+"F0.imprint","IMPRINT",FACE,{"disambiguationData":[TD([[makeQuery(id+"F0.imprint","IMPRINT",EDGE,{"derivedFrom":sQuery(id+"F0.wireOp",EDGE,"E10.7.0.0")}),1.0]])]});
            var Q40;
            Q40=makeQuery(id+"F0.imprint","IMPRINT",FACE,{"disambiguationData":[TD([[makeQuery(id+"F0.imprint","IMPRINT",EDGE,{"derivedFrom":sQuery(id+"F0.wireOp",EDGE,"E10.6.0.0")}),1.0]])]});
            var Q41;
            Q41=makeQuery(id+"F0.imprint","IMPRINT",FACE,{"disambiguationData":[TD([[makeQuery(id+"F0.imprint","IMPRINT",EDGE,{"derivedFrom":sQuery(id+"F0.wireOp",EDGE,"E10.5.0.0")}),1.0]])]});
            var Q42;
            Q42=makeQuery(id+"F0.imprint","IMPRINT",FACE,{"disambiguationData":[TD([[makeQuery(id+"F0.imprint","IMPRINT",EDGE,{"derivedFrom":sQuery(id+"F0.wireOp",EDGE,"E16.5.0.0")}),-1.0]])]});
            var Q43;
            Q43=makeQuery(id+"F0.imprint","IMPRINT",FACE,{"disambiguationData":[TD([[makeQuery(id+"F0.imprint","IMPRINT",EDGE,{"derivedFrom":sQuery(id+"F0.wireOp",EDGE,"E16.6.0.0")}),-1.0]])]});
            var Q44;
            Q44=makeQuery(id+"F0.imprint","IMPRINT",FACE,{"disambiguationData":[TD([[makeQuery(id+"F0.imprint","IMPRINT",EDGE,{"derivedFrom":sQuery(id+"F0.wireOp",EDGE,"E16.7.0.0")}),-1.0]])]});
            var Q45;
            Q45=makeQuery(id+"F0.imprint","IMPRINT",FACE,{"disambiguationData":[TD([[makeQuery(id+"F0.imprint","IMPRINT",EDGE,{"derivedFrom":sQuery(id+"F0.wireOp",EDGE,"E19.7.0.0")}),-1.0]])]});
            var Q46;
            Q46=makeQuery(id+"F0.imprint","IMPRINT",FACE,{"disambiguationData":[TD([[makeQuery(id+"F0.imprint","IMPRINT",EDGE,{"derivedFrom":sQuery(id+"F0.wireOp",EDGE,"E19.6.0.0")}),-1.0]])]});
            var Q47;
            Q47=makeQuery(id+"F0.imprint","IMPRINT",FACE,{"disambiguationData":[TD([[makeQuery(id+"F0.imprint","IMPRINT",EDGE,{"derivedFrom":sQuery(id+"F0.wireOp",EDGE,"E19.5.0.0")}),-1.0]])]});
            var Q48;
            Q48=makeQuery(id+"F0.imprint","IMPRINT",FACE,{"disambiguationData":[TD([[makeQuery(id+"F0.imprint","IMPRINT",EDGE,{"derivedFrom":sQuery(id+"F0.wireOp",EDGE,"E22.5.0.0")}),-1.0]])]});
            var Q49;
            Q49=makeQuery(id+"F0.imprint","IMPRINT",FACE,{"disambiguationData":[TD([[makeQuery(id+"F0.imprint","IMPRINT",EDGE,{"derivedFrom":sQuery(id+"F0.wireOp",EDGE,"E22.6.0.0")}),-1.0]])]});
            var Q50;
            Q50=makeQuery(id+"F0.imprint","IMPRINT",FACE,{"disambiguationData":[TD([[makeQuery(id+"F0.imprint","IMPRINT",EDGE,{"derivedFrom":sQuery(id+"F0.wireOp",EDGE,"E27.5.0.0")}),-1.0]])]});
            var Q51;
            Q51=makeQuery(id+"F0.imprint","IMPRINT",FACE,{"disambiguationData":[TD([[makeQuery(id+"F0.imprint","IMPRINT",EDGE,{"derivedFrom":sQuery(id+"F0.wireOp",EDGE,"E27.6.0.0")}),-1.0]])]});
            var Q52;
            Q52=makeQuery(id+"F0.imprint","IMPRINT",FACE,{"disambiguationData":[TD([[makeQuery(id+"F0.imprint","IMPRINT",EDGE,{"derivedFrom":sQuery(id+"F0.wireOp",EDGE,"E27.7.0.0")}),-1.0]])]});
            var Q53;
            Q53=makeQuery(id+"F0.imprint","IMPRINT",FACE,{"disambiguationData":[TD([[makeQuery(id+"F0.imprint","IMPRINT",EDGE,{"derivedFrom":sQuery(id+"F0.wireOp",EDGE,"E22.7.0.0")}),-1.0]])]});
            var Q54;
            Q54=makeQuery(id+"F0.imprint","IMPRINT",FACE,{"disambiguationData":[TD([[makeQuery(id+"F0.imprint","IMPRINT",EDGE,{"derivedFrom":sQuery(id+"F0.wireOp",EDGE,"E28.7.0.0")}),-1.0]])]});
            var Q55;
            Q55=makeQuery(id+"F0.imprint","IMPRINT",FACE,{"disambiguationData":[TD([[makeQuery(id+"F0.imprint","IMPRINT",EDGE,{"derivedFrom":sQuery(id+"F0.wireOp",EDGE,"E28.6.0.0")}),-1.0]])]});
            var Q56;
            Q56=makeQuery(id+"F0.imprint","IMPRINT",FACE,{"disambiguationData":[TD([[makeQuery(id+"F0.imprint","IMPRINT",EDGE,{"derivedFrom":sQuery(id+"F0.wireOp",EDGE,"E28.5.0.0")}),-1.0]])]});
            var Q57;
            Q57=makeQuery(id+"F0.imprint","IMPRINT",FACE,{"disambiguationData":[TD([[makeQuery(id+"F0.imprint","IMPRINT",EDGE,{"derivedFrom":sQuery(id+"F0.wireOp",EDGE,"E16.12.0.0")}),-1.0]])]});
            var Q58;
            Q58=makeQuery(id+"F0.imprint","IMPRINT",FACE,{"disambiguationData":[TD([[makeQuery(id+"F0.imprint","IMPRINT",EDGE,{"derivedFrom":sQuery(id+"F0.wireOp",EDGE,"E10.12.0.0")}),1.0]])]});
            var Q59;
            Q59=makeQuery(id+"F0.imprint","IMPRINT",FACE,{"disambiguationData":[TD([[makeQuery(id+"F0.imprint","IMPRINT",EDGE,{"derivedFrom":sQuery(id+"F0.wireOp",EDGE,"E10.11.0.0")}),1.0]])]});
            var Q60;
            Q60=makeQuery(id+"F0.imprint","IMPRINT",FACE,{"disambiguationData":[TD([[makeQuery(id+"F0.imprint","IMPRINT",EDGE,{"derivedFrom":sQuery(id+"F0.wireOp",EDGE,"E10.10.0.0")}),1.0]])]});
            var Q61;
            Q61=makeQuery(id+"F0.imprint","IMPRINT",FACE,{"disambiguationData":[TD([[makeQuery(id+"F0.imprint","IMPRINT",EDGE,{"derivedFrom":sQuery(id+"F0.wireOp",EDGE,"E16.10.0.0")}),-1.0]])]});
            var Q62;
            Q62=makeQuery(id+"F0.imprint","IMPRINT",FACE,{"disambiguationData":[TD([[makeQuery(id+"F0.imprint","IMPRINT",EDGE,{"derivedFrom":sQuery(id+"F0.wireOp",EDGE,"E19.10.0.0")}),-1.0]])]});
            var Q63;
            Q63=makeQuery(id+"F0.imprint","IMPRINT",FACE,{"disambiguationData":[TD([[makeQuery(id+"F0.imprint","IMPRINT",EDGE,{"derivedFrom":sQuery(id+"F0.wireOp",EDGE,"E16.11.0.0")}),-1.0]])]});
            var Q64;
            Q64=makeQuery(id+"F0.imprint","IMPRINT",FACE,{"disambiguationData":[TD([[makeQuery(id+"F0.imprint","IMPRINT",EDGE,{"derivedFrom":sQuery(id+"F0.wireOp",EDGE,"E19.11.0.0")}),-1.0]])]});
            var Q65;
            Q65=makeQuery(id+"F0.imprint","IMPRINT",FACE,{"disambiguationData":[TD([[makeQuery(id+"F0.imprint","IMPRINT",EDGE,{"derivedFrom":sQuery(id+"F0.wireOp",EDGE,"E22.11.0.0")}),-1.0]])]});
            var Q66;
            Q66=makeQuery(id+"F0.imprint","IMPRINT",FACE,{"disambiguationData":[TD([[makeQuery(id+"F0.imprint","IMPRINT",EDGE,{"derivedFrom":sQuery(id+"F0.wireOp",EDGE,"E22.12.0.0")}),-1.0]])]});
            var Q67;
            Q67=makeQuery(id+"F0.imprint","IMPRINT",FACE,{"disambiguationData":[TD([[makeQuery(id+"F0.imprint","IMPRINT",EDGE,{"derivedFrom":sQuery(id+"F0.wireOp",EDGE,"E22.13.0.0")}),-1.0]])]});
            var Q68;
            Q68=makeQuery(id+"F0.imprint","IMPRINT",FACE,{"disambiguationData":[TD([[makeQuery(id+"F0.imprint","IMPRINT",EDGE,{"derivedFrom":sQuery(id+"F0.wireOp",EDGE,"E19.13.0.0")}),-1.0]])]});
            var Q69;
            Q69=makeQuery(id+"F0.imprint","IMPRINT",FACE,{"disambiguationData":[TD([[makeQuery(id+"F0.imprint","IMPRINT",EDGE,{"derivedFrom":sQuery(id+"F0.wireOp",EDGE,"E19.12.0.0")}),-1.0]])]});
            var Q70;
            Q70=makeQuery(id+"F0.imprint","IMPRINT",FACE,{"disambiguationData":[TD([[makeQuery(id+"F0.imprint","IMPRINT",EDGE,{"derivedFrom":sQuery(id+"F0.wireOp",EDGE,"E16.13.0.0")}),-1.0]])]});
            var Q71;
            Q71=makeQuery(id+"F0.imprint","IMPRINT",FACE,{"disambiguationData":[TD([[makeQuery(id+"F0.imprint","IMPRINT",EDGE,{"derivedFrom":sQuery(id+"F0.wireOp",EDGE,"E10.13.0.0")}),1.0]])]});
            var Q72;
            Q72=makeQuery(id+"F0.imprint","IMPRINT",FACE,{"disambiguationData":[TD([[makeQuery(id+"F0.imprint","IMPRINT",EDGE,{"derivedFrom":sQuery(id+"F0.wireOp",EDGE,"E13.13.0.0")}),1.0]])]});
            var Q73;
            Q73=makeQuery(id+"F0.imprint","IMPRINT",FACE,{"disambiguationData":[TD([[makeQuery(id+"F0.imprint","IMPRINT",EDGE,{"derivedFrom":sQuery(id+"F0.wireOp",EDGE,"E13.12.0.0")}),1.0]])]});
            var Q74;
            Q74=makeQuery(id+"F0.imprint","IMPRINT",FACE,{"disambiguationData":[TD([[makeQuery(id+"F0.imprint","IMPRINT",EDGE,{"derivedFrom":sQuery(id+"F0.wireOp",EDGE,"E13.11.0.0")}),1.0]])]});
            var Q75;
            Q75=makeQuery(id+"F0.imprint","IMPRINT",FACE,{"disambiguationData":[TD([[makeQuery(id+"F0.imprint","IMPRINT",EDGE,{"derivedFrom":sQuery(id+"F0.wireOp",EDGE,"E10.14.0.0")}),1.0]])]});
            var Q76;
            Q76=makeQuery(id+"F0.imprint","IMPRINT",FACE,{"disambiguationData":[TD([[makeQuery(id+"F0.imprint","IMPRINT",EDGE,{"derivedFrom":sQuery(id+"F0.wireOp",EDGE,"E22.14.0.0")}),-1.0]])]});
            var Q77;
            Q77=makeQuery(id+"F0.imprint","IMPRINT",FACE,{"disambiguationData":[TD([[makeQuery(id+"F0.imprint","IMPRINT",EDGE,{"derivedFrom":sQuery(id+"F0.wireOp",EDGE,"E27.13.0.0")}),-1.0]])]});
            var Q78;
            Q78=makeQuery(id+"F0.imprint","IMPRINT",FACE,{"disambiguationData":[TD([[makeQuery(id+"F0.imprint","IMPRINT",EDGE,{"derivedFrom":sQuery(id+"F0.wireOp",EDGE,"E13.14.0.0")}),1.0]])]});
            var Q79;
            Q79=makeQuery(id+"F0.imprint","IMPRINT",FACE,{"disambiguationData":[TD([[makeQuery(id+"F0.imprint","IMPRINT",EDGE,{"derivedFrom":sQuery(id+"F0.wireOp",EDGE,"E13.10.0.0")}),1.0]])]});
            var Q80;
            Q80=makeQuery(id+"F0.imprint","IMPRINT",FACE,{"disambiguationData":[TD([[makeQuery(id+"F0.imprint","IMPRINT",EDGE,{"derivedFrom":sQuery(id+"F0.wireOp",EDGE,"E13.9.0.0")}),1.0]])]});
            var Q81;
            Q81=makeQuery(id+"F0.imprint","IMPRINT",FACE,{"disambiguationData":[TD([[makeQuery(id+"F0.imprint","IMPRINT",EDGE,{"derivedFrom":sQuery(id+"F0.wireOp",EDGE,"E13.8.0.0")}),1.0]])]});
            var Q82;
            Q82=makeQuery(id+"F0.imprint","IMPRINT",FACE,{"disambiguationData":[TD([[makeQuery(id+"F0.imprint","IMPRINT",EDGE,{"derivedFrom":sQuery(id+"F0.wireOp",EDGE,"E10.8.0.0")}),1.0]])]});
            var Q83;
            Q83=makeQuery(id+"F0.imprint","IMPRINT",FACE,{"disambiguationData":[TD([[makeQuery(id+"F0.imprint","IMPRINT",EDGE,{"derivedFrom":sQuery(id+"F0.wireOp",EDGE,"E10.9.0.0")}),1.0]])]});
            var Q84;
            Q84=makeQuery(id+"F0.imprint","IMPRINT",FACE,{"disambiguationData":[TD([[makeQuery(id+"F0.imprint","IMPRINT",EDGE,{"derivedFrom":sQuery(id+"F0.wireOp",EDGE,"E22.8.0.0")}),-1.0]])]});
            var Q85;
            Q85=makeQuery(id+"F0.imprint","IMPRINT",FACE,{"disambiguationData":[TD([[makeQuery(id+"F0.imprint","IMPRINT",EDGE,{"derivedFrom":sQuery(id+"F0.wireOp",EDGE,"E22.9.0.0")}),-1.0]])]});
            var Q86;
            Q86=makeQuery(id+"F0.imprint","IMPRINT",FACE,{"disambiguationData":[TD([[makeQuery(id+"F0.imprint","IMPRINT",EDGE,{"derivedFrom":sQuery(id+"F0.wireOp",EDGE,"E19.9.0.0")}),-1.0]])]});
            var Q87;
            Q87=makeQuery(id+"F0.imprint","IMPRINT",FACE,{"disambiguationData":[TD([[makeQuery(id+"F0.imprint","IMPRINT",EDGE,{"derivedFrom":sQuery(id+"F0.wireOp",EDGE,"E16.9.0.0")}),-1.0]])]});
            var Q88;
            Q88=makeQuery(id+"F0.imprint","IMPRINT",FACE,{"disambiguationData":[TD([[makeQuery(id+"F0.imprint","IMPRINT",EDGE,{"derivedFrom":sQuery(id+"F0.wireOp",EDGE,"E16.8.0.0")}),-1.0]])]});
            var Q89;
            Q89=makeQuery(id+"F0.imprint","IMPRINT",FACE,{"disambiguationData":[TD([[makeQuery(id+"F0.imprint","IMPRINT",EDGE,{"derivedFrom":sQuery(id+"F0.wireOp",EDGE,"E19.8.0.0")}),-1.0]])]});
            var Q90;
            Q90=makeQuery(id+"F0.imprint","IMPRINT",FACE,{"disambiguationData":[TD([[makeQuery(id+"F0.imprint","IMPRINT",EDGE,{"derivedFrom":sQuery(id+"F0.wireOp",EDGE,"E22.10.0.0")}),-1.0]])]});
            var Q91;
            Q91=makeQuery(id+"F0.imprint","IMPRINT",FACE,{"disambiguationData":[TD([[makeQuery(id+"F0.imprint","IMPRINT",EDGE,{"derivedFrom":sQuery(id+"F0.wireOp",EDGE,"E28.10.0.0")}),-1.0]])]});
            var Q92;
            Q92=makeQuery(id+"F0.imprint","IMPRINT",FACE,{"disambiguationData":[TD([[makeQuery(id+"F0.imprint","IMPRINT",EDGE,{"derivedFrom":sQuery(id+"F0.wireOp",EDGE,"E28.11.0.0")}),-1.0]])]});
            var Q93;
            Q93=makeQuery(id+"F0.imprint","IMPRINT",FACE,{"disambiguationData":[TD([[makeQuery(id+"F0.imprint","IMPRINT",EDGE,{"derivedFrom":sQuery(id+"F0.wireOp",EDGE,"E27.11.0.0")}),-1.0]])]});
            var Q94;
            Q94=makeQuery(id+"F0.imprint","IMPRINT",FACE,{"disambiguationData":[TD([[makeQuery(id+"F0.imprint","IMPRINT",EDGE,{"derivedFrom":sQuery(id+"F0.wireOp",EDGE,"E27.10.0.0")}),-1.0]])]});
            var Q95;
            Q95=makeQuery(id+"F0.imprint","IMPRINT",FACE,{"disambiguationData":[TD([[makeQuery(id+"F0.imprint","IMPRINT",EDGE,{"derivedFrom":sQuery(id+"F0.wireOp",EDGE,"E27.9.0.0")}),-1.0]])]});
            var Q96;
            Q96=makeQuery(id+"F0.imprint","IMPRINT",FACE,{"disambiguationData":[TD([[makeQuery(id+"F0.imprint","IMPRINT",EDGE,{"derivedFrom":sQuery(id+"F0.wireOp",EDGE,"E27.8.0.0")}),-1.0]])]});
            var Q97;
            Q97=makeQuery(id+"F0.imprint","IMPRINT",FACE,{"disambiguationData":[TD([[makeQuery(id+"F0.imprint","IMPRINT",EDGE,{"derivedFrom":sQuery(id+"F0.wireOp",EDGE,"E28.9.0.0")}),-1.0]])]});
            var Q98;
            Q98=makeQuery(id+"F0.imprint","IMPRINT",FACE,{"disambiguationData":[TD([[makeQuery(id+"F0.imprint","IMPRINT",EDGE,{"derivedFrom":sQuery(id+"F0.wireOp",EDGE,"E28.8.0.0")}),-1.0]])]});
            var Q99;
            Q99=makeQuery(id+"F0.imprint","IMPRINT",FACE,{"disambiguationData":[TD([[makeQuery(id+"F0.imprint","IMPRINT",EDGE,{"derivedFrom":sQuery(id+"F0.wireOp",EDGE,"E28.12.0.0")}),-1.0]])]});
            var Q100;
            Q100=makeQuery(id+"F0.imprint","IMPRINT",FACE,{"disambiguationData":[TD([[makeQuery(id+"F0.imprint","IMPRINT",EDGE,{"derivedFrom":sQuery(id+"F0.wireOp",EDGE,"E27.12.0.0")}),-1.0]])]});
            var Q101;
            Q101=makeQuery(id+"F0.imprint","IMPRINT",FACE,{"disambiguationData":[TD([[makeQuery(id+"F0.imprint","IMPRINT",EDGE,{"derivedFrom":sQuery(id+"F0.wireOp",EDGE,"E28.13.0.0")}),-1.0]])]});
            var Q102;
            Q102=makeQuery(id+"F0.imprint","IMPRINT",FACE,{"disambiguationData":[TD([[makeQuery(id+"F0.imprint","IMPRINT",EDGE,{"derivedFrom":sQuery(id+"F0.wireOp",EDGE,"E28.14.0.0")}),-1.0]])]});
            var Q103;
            Q103=makeQuery(id+"F0.imprint","IMPRINT",FACE,{"disambiguationData":[TD([[makeQuery(id+"F0.imprint","IMPRINT",EDGE,{"derivedFrom":sQuery(id+"F0.wireOp",EDGE,"E27.14.0.0")}),-1.0]])]});
            var Q104;
            Q104=makeQuery(id+"F0.imprint","IMPRINT",FACE,{"disambiguationData":[TD([[makeQuery(id+"F0.imprint","IMPRINT",EDGE,{"derivedFrom":sQuery(id+"F0.wireOp",EDGE,"E19.14.0.0")}),-1.0]])]});
            var Q105;
            Q105=makeQuery(id+"F0.imprint","IMPRINT",FACE,{"disambiguationData":[TD([[makeQuery(id+"F0.imprint","IMPRINT",EDGE,{"derivedFrom":sQuery(id+"F0.wireOp",EDGE,"E16.14.0.0")}),-1.0]])]});
            extrude(context, id + "F3", {"entities" : qUnion([Q0, Q1, Q2, Q3, Q4, Q5, Q6, Q7, Q8, Q9, Q10, Q11, Q12, Q13, Q14, Q15, Q16, Q17, Q18, Q19, Q20, Q21, Q22, Q23, Q24, Q25, Q26, Q27, Q28, Q29, Q30, Q31, Q32, Q33, Q34, Q35, Q36, Q37, Q38, Q39, Q40, Q41, Q42, Q43, Q44, Q45, Q46, Q47, Q48, Q49, Q50, Q51, Q52, Q53, Q54, Q55, Q56, Q57, Q58, Q59, Q60, Q61, Q62, Q63, Q64, Q65, Q66, Q67, Q68, Q69, Q70, Q71, Q72, Q73, Q74, Q75, Q76, Q77, Q78, Q79, Q80, Q81, Q82, Q83, Q84, Q85, Q86, Q87, Q88, Q89, Q90, Q91, Q92, Q93, Q94, Q95, Q96, Q97, Q98, Q99, Q100, Q101, Q102, Q103, Q104, Q105]), "operationType" : NewBodyOperationType.ADD, "depth" : 3.2 * mm, "offsetDistance" : 25.4 * mm});
        }
        {
            var Q0;
            Q0=makeQuery(id+"F0.imprint","IMPRINT",FACE,{"disambiguationData":[TD([[makeQuery(id+"F0.imprint","IMPRINT",EDGE,{"derivedFrom":sQuery(id+"F0.wireOp",EDGE,"E19.8.0.0")}),1.0]])]});
            var Q1;
            Q1=makeQuery(id+"F0.imprint","IMPRINT",FACE,{"disambiguationData":[TD([[makeQuery(id+"F0.imprint","IMPRINT",EDGE,{"derivedFrom":sQuery(id+"F0.wireOp",EDGE,"E16.8.0.0")}),1.0]])]});
            var Q2;
            Q2=makeQuery(id+"F0.imprint","IMPRINT",FACE,{"disambiguationData":[TD([[makeQuery(id+"F0.imprint","IMPRINT",EDGE,{"derivedFrom":sQuery(id+"F0.wireOp",EDGE,"E16.7.0.0")}),1.0]])]});
            var Q3;
            Q3=makeQuery(id+"F0.imprint","IMPRINT",FACE,{"disambiguationData":[TD([[makeQuery(id+"F0.imprint","IMPRINT",EDGE,{"derivedFrom":sQuery(id+"F0.wireOp",EDGE,"E19.7.0.0")}),1.0]])]});
            var Q4;
            Q4=makeQuery(id+"F0.imprint","IMPRINT",FACE,{"disambiguationData":[TD([[makeQuery(id+"F0.imprint","IMPRINT",EDGE,{"derivedFrom":sQuery(id+"F0.wireOp",EDGE,"E22.7.0.0")}),1.0]])]});
            var Q5;
            Q5=makeQuery(id+"F0.imprint","IMPRINT",FACE,{"disambiguationData":[TD([[makeQuery(id+"F0.imprint","IMPRINT",EDGE,{"derivedFrom":sQuery(id+"F0.wireOp",EDGE,"E27.7.0.0")}),1.0]])]});
            var Q6;
            Q6=makeQuery(id+"F0.imprint","IMPRINT",FACE,{"disambiguationData":[TD([[makeQuery(id+"F0.imprint","IMPRINT",EDGE,{"derivedFrom":sQuery(id+"F0.wireOp",EDGE,"E22.8.0.0")}),1.0]])]});
            var Q7;
            Q7=makeQuery(id+"F0.imprint","IMPRINT",FACE,{"disambiguationData":[TD([[makeQuery(id+"F0.imprint","IMPRINT",EDGE,{"derivedFrom":sQuery(id+"F0.wireOp",EDGE,"E27.8.0.0")}),1.0]])]});
            var Q8;
            Q8=makeQuery(id+"F0.imprint","IMPRINT",FACE,{"disambiguationData":[TD([[makeQuery(id+"F0.imprint","IMPRINT",EDGE,{"derivedFrom":sQuery(id+"F0.wireOp",EDGE,"E28.8.0.0")}),1.0]])]});
            var Q9;
            Q9=makeQuery(id+"F0.imprint","IMPRINT",FACE,{"disambiguationData":[TD([[makeQuery(id+"F0.imprint","IMPRINT",EDGE,{"derivedFrom":sQuery(id+"F0.wireOp",EDGE,"E28.7.0.0")}),1.0]])]});
            var Q10;
            Q10=makeQuery(id+"F0.imprint","IMPRINT",FACE,{"disambiguationData":[TD([[makeQuery(id+"F0.imprint","IMPRINT",EDGE,{"derivedFrom":sQuery(id+"F0.wireOp",EDGE,"E28.6.0.0")}),1.0]])]});
            var Q11;
            Q11=makeQuery(id+"F0.imprint","IMPRINT",FACE,{"disambiguationData":[TD([[makeQuery(id+"F0.imprint","IMPRINT",EDGE,{"derivedFrom":sQuery(id+"F0.wireOp",EDGE,"E27.6.0.0")}),1.0]])]});
            var Q12;
            Q12=makeQuery(id+"F0.imprint","IMPRINT",FACE,{"disambiguationData":[TD([[makeQuery(id+"F0.imprint","IMPRINT",EDGE,{"derivedFrom":sQuery(id+"F0.wireOp",EDGE,"E22.6.0.0")}),1.0]])]});
            var Q13;
            Q13=makeQuery(id+"F0.imprint","IMPRINT",FACE,{"disambiguationData":[TD([[makeQuery(id+"F0.imprint","IMPRINT",EDGE,{"derivedFrom":sQuery(id+"F0.wireOp",EDGE,"E19.6.0.0")}),1.0]])]});
            var Q14;
            Q14=makeQuery(id+"F0.imprint","IMPRINT",FACE,{"disambiguationData":[TD([[makeQuery(id+"F0.imprint","IMPRINT",EDGE,{"derivedFrom":sQuery(id+"F0.wireOp",EDGE,"E16.6.0.0")}),1.0]])]});
            var Q15;
            Q15=makeQuery(id+"F0.imprint","IMPRINT",FACE,{"disambiguationData":[TD([[makeQuery(id+"F0.imprint","IMPRINT",EDGE,{"derivedFrom":sQuery(id+"F0.wireOp",EDGE,"E10.6.0.1")}),1.0]])]});
            var Q16;
            Q16=makeQuery(id+"F0.imprint","IMPRINT",FACE,{"disambiguationData":[TD([[makeQuery(id+"F0.imprint","IMPRINT",EDGE,{"derivedFrom":sQuery(id+"F0.wireOp",EDGE,"E10.7.0.1")}),1.0]])]});
            var Q17;
            Q17=makeQuery(id+"F0.imprint","IMPRINT",FACE,{"disambiguationData":[TD([[makeQuery(id+"F0.imprint","IMPRINT",EDGE,{"derivedFrom":sQuery(id+"F0.wireOp",EDGE,"E10.8.0.1")}),1.0]])]});
            var Q18;
            Q18=makeQuery(id+"F0.imprint","IMPRINT",FACE,{"disambiguationData":[TD([[makeQuery(id+"F0.imprint","IMPRINT",EDGE,{"derivedFrom":sQuery(id+"F0.wireOp",EDGE,"E10.9.0.1")}),1.0]])]});
            var Q19;
            Q19=makeQuery(id+"F0.imprint","IMPRINT",FACE,{"disambiguationData":[TD([[makeQuery(id+"F0.imprint","IMPRINT",EDGE,{"derivedFrom":sQuery(id+"F0.wireOp",EDGE,"E16.9.0.0")}),1.0]])]});
            var Q20;
            Q20=makeQuery(id+"F0.imprint","IMPRINT",FACE,{"disambiguationData":[TD([[makeQuery(id+"F0.imprint","IMPRINT",EDGE,{"derivedFrom":sQuery(id+"F0.wireOp",EDGE,"E19.9.0.0")}),1.0]])]});
            var Q21;
            Q21=makeQuery(id+"F0.imprint","IMPRINT",FACE,{"disambiguationData":[TD([[makeQuery(id+"F0.imprint","IMPRINT",EDGE,{"derivedFrom":sQuery(id+"F0.wireOp",EDGE,"E22.9.0.0")}),1.0]])]});
            var Q22;
            Q22=makeQuery(id+"F0.imprint","IMPRINT",FACE,{"disambiguationData":[TD([[makeQuery(id+"F0.imprint","IMPRINT",EDGE,{"derivedFrom":sQuery(id+"F0.wireOp",EDGE,"E27.9.0.0")}),1.0]])]});
            var Q23;
            Q23=makeQuery(id+"F0.imprint","IMPRINT",FACE,{"disambiguationData":[TD([[makeQuery(id+"F0.imprint","IMPRINT",EDGE,{"derivedFrom":sQuery(id+"F0.wireOp",EDGE,"E28.9.0.0")}),1.0]])]});
            var Q24;
            Q24=makeQuery(id+"F0.imprint","IMPRINT",FACE,{"disambiguationData":[TD([[makeQuery(id+"F0.imprint","IMPRINT",EDGE,{"derivedFrom":sQuery(id+"F0.wireOp",EDGE,"E28.5.0.0")}),1.0]])]});
            var Q25;
            Q25=makeQuery(id+"F0.imprint","IMPRINT",FACE,{"disambiguationData":[TD([[makeQuery(id+"F0.imprint","IMPRINT",EDGE,{"derivedFrom":sQuery(id+"F0.wireOp",EDGE,"E27.5.0.0")}),1.0]])]});
            var Q26;
            Q26=makeQuery(id+"F0.imprint","IMPRINT",FACE,{"disambiguationData":[TD([[makeQuery(id+"F0.imprint","IMPRINT",EDGE,{"derivedFrom":sQuery(id+"F0.wireOp",EDGE,"E22.5.0.0")}),1.0]])]});
            var Q27;
            Q27=makeQuery(id+"F0.imprint","IMPRINT",FACE,{"disambiguationData":[TD([[makeQuery(id+"F0.imprint","IMPRINT",EDGE,{"derivedFrom":sQuery(id+"F0.wireOp",EDGE,"E19.5.0.0")}),1.0]])]});
            var Q28;
            Q28=makeQuery(id+"F0.imprint","IMPRINT",FACE,{"disambiguationData":[TD([[makeQuery(id+"F0.imprint","IMPRINT",EDGE,{"derivedFrom":sQuery(id+"F0.wireOp",EDGE,"E16.5.0.0")}),1.0]])]});
            var Q29;
            Q29=makeQuery(id+"F0.imprint","IMPRINT",FACE,{"disambiguationData":[TD([[makeQuery(id+"F0.imprint","IMPRINT",EDGE,{"derivedFrom":sQuery(id+"F0.wireOp",EDGE,"E10.5.0.1")}),1.0]])]});
            var Q30;
            Q30=makeQuery(id+"F0.imprint","IMPRINT",FACE,{"disambiguationData":[TD([[makeQuery(id+"F0.imprint","IMPRINT",EDGE,{"derivedFrom":sQuery(id+"F0.wireOp",EDGE,"E10.4.0.1")}),1.0]])]});
            var Q31;
            Q31=makeQuery(id+"F0.imprint","IMPRINT",FACE,{"disambiguationData":[TD([[makeQuery(id+"F0.imprint","IMPRINT",EDGE,{"derivedFrom":sQuery(id+"F0.wireOp",EDGE,"E16.4.0.0")}),1.0]])]});
            var Q32;
            Q32=makeQuery(id+"F0.imprint","IMPRINT",FACE,{"disambiguationData":[TD([[makeQuery(id+"F0.imprint","IMPRINT",EDGE,{"derivedFrom":sQuery(id+"F0.wireOp",EDGE,"E19.4.0.0")}),1.0]])]});
            var Q33;
            Q33=makeQuery(id+"F0.imprint","IMPRINT",FACE,{"disambiguationData":[TD([[makeQuery(id+"F0.imprint","IMPRINT",EDGE,{"derivedFrom":sQuery(id+"F0.wireOp",EDGE,"E22.4.0.0")}),1.0]])]});
            var Q34;
            Q34=makeQuery(id+"F0.imprint","IMPRINT",FACE,{"disambiguationData":[TD([[makeQuery(id+"F0.imprint","IMPRINT",EDGE,{"derivedFrom":sQuery(id+"F0.wireOp",EDGE,"E27.4.0.0")}),1.0]])]});
            var Q35;
            Q35=makeQuery(id+"F0.imprint","IMPRINT",FACE,{"disambiguationData":[TD([[makeQuery(id+"F0.imprint","IMPRINT",EDGE,{"derivedFrom":sQuery(id+"F0.wireOp",EDGE,"E28.4.0.0")}),1.0]])]});
            var Q36;
            Q36=makeQuery(id+"F0.imprint","IMPRINT",FACE,{"disambiguationData":[TD([[makeQuery(id+"F0.imprint","IMPRINT",EDGE,{"derivedFrom":sQuery(id+"F0.wireOp",EDGE,"E28.3.0.0")}),1.0]])]});
            var Q37;
            Q37=makeQuery(id+"F0.imprint","IMPRINT",FACE,{"disambiguationData":[TD([[makeQuery(id+"F0.imprint","IMPRINT",EDGE,{"derivedFrom":sQuery(id+"F0.wireOp",EDGE,"E27.3.0.0")}),1.0]])]});
            var Q38;
            Q38=makeQuery(id+"F0.imprint","IMPRINT",FACE,{"disambiguationData":[TD([[makeQuery(id+"F0.imprint","IMPRINT",EDGE,{"derivedFrom":sQuery(id+"F0.wireOp",EDGE,"E22.3.0.0")}),1.0]])]});
            var Q39;
            Q39=makeQuery(id+"F0.imprint","IMPRINT",FACE,{"disambiguationData":[TD([[makeQuery(id+"F0.imprint","IMPRINT",EDGE,{"derivedFrom":sQuery(id+"F0.wireOp",EDGE,"E27.2.0.0")}),1.0]])]});
            var Q40;
            Q40=makeQuery(id+"F0.imprint","IMPRINT",FACE,{"disambiguationData":[TD([[makeQuery(id+"F0.imprint","IMPRINT",EDGE,{"derivedFrom":sQuery(id+"F0.wireOp",EDGE,"E28.2.0.0")}),1.0]])]});
            var Q41;
            Q41=makeQuery(id+"F0.imprint","IMPRINT",FACE,{"disambiguationData":[TD([[makeQuery(id+"F0.imprint","IMPRINT",EDGE,{"derivedFrom":sQuery(id+"F0.wireOp",EDGE,"E16.2.0.0")}),1.0]])]});
            var Q42;
            Q42=makeQuery(id+"F0.imprint","IMPRINT",FACE,{"disambiguationData":[TD([[makeQuery(id+"F0.imprint","IMPRINT",EDGE,{"derivedFrom":sQuery(id+"F0.wireOp",EDGE,"E10.2.0.1")}),1.0]])]});
            var Q43;
            Q43=makeQuery(id+"F0.imprint","IMPRINT",FACE,{"disambiguationData":[TD([[makeQuery(id+"F0.imprint","IMPRINT",EDGE,{"derivedFrom":sQuery(id+"F0.wireOp",EDGE,"E10.3.0.1")}),1.0]])]});
            var Q44;
            Q44=makeQuery(id+"F0.imprint","IMPRINT",FACE,{"disambiguationData":[TD([[makeQuery(id+"F0.imprint","IMPRINT",EDGE,{"derivedFrom":sQuery(id+"F0.wireOp",EDGE,"E28.10.0.0")}),1.0]])]});
            var Q45;
            Q45=makeQuery(id+"F0.imprint","IMPRINT",FACE,{"disambiguationData":[TD([[makeQuery(id+"F0.imprint","IMPRINT",EDGE,{"derivedFrom":sQuery(id+"F0.wireOp",EDGE,"E27.10.0.0")}),1.0]])]});
            var Q46;
            Q46=makeQuery(id+"F0.imprint","IMPRINT",FACE,{"disambiguationData":[TD([[makeQuery(id+"F0.imprint","IMPRINT",EDGE,{"derivedFrom":sQuery(id+"F0.wireOp",EDGE,"E22.10.0.0")}),1.0]])]});
            var Q47;
            Q47=makeQuery(id+"F0.imprint","IMPRINT",FACE,{"disambiguationData":[TD([[makeQuery(id+"F0.imprint","IMPRINT",EDGE,{"derivedFrom":sQuery(id+"F0.wireOp",EDGE,"E19.10.0.0")}),1.0]])]});
            var Q48;
            Q48=makeQuery(id+"F0.imprint","IMPRINT",FACE,{"disambiguationData":[TD([[makeQuery(id+"F0.imprint","IMPRINT",EDGE,{"derivedFrom":sQuery(id+"F0.wireOp",EDGE,"E16.10.0.0")}),1.0]])]});
            var Q49;
            Q49=makeQuery(id+"F0.imprint","IMPRINT",FACE,{"disambiguationData":[TD([[makeQuery(id+"F0.imprint","IMPRINT",EDGE,{"derivedFrom":sQuery(id+"F0.wireOp",EDGE,"E10.10.0.1")}),1.0]])]});
            var Q50;
            Q50=makeQuery(id+"F0.imprint","IMPRINT",FACE,{"disambiguationData":[TD([[makeQuery(id+"F0.imprint","IMPRINT",EDGE,{"derivedFrom":sQuery(id+"F0.wireOp",EDGE,"E13.10.0.1")}),1.0]])]});
            var Q51;
            Q51=makeQuery(id+"F0.imprint","IMPRINT",FACE,{"disambiguationData":[TD([[makeQuery(id+"F0.imprint","IMPRINT",EDGE,{"derivedFrom":sQuery(id+"F0.wireOp",EDGE,"E13.11.0.1")}),1.0]])]});
            var Q52;
            Q52=makeQuery(id+"F0.imprint","IMPRINT",FACE,{"disambiguationData":[TD([[makeQuery(id+"F0.imprint","IMPRINT",EDGE,{"derivedFrom":sQuery(id+"F0.wireOp",EDGE,"E13.12.0.1")}),1.0]])]});
            var Q53;
            Q53=makeQuery(id+"F0.imprint","IMPRINT",FACE,{"disambiguationData":[TD([[makeQuery(id+"F0.imprint","IMPRINT",EDGE,{"derivedFrom":sQuery(id+"F0.wireOp",EDGE,"E13.13.0.1")}),1.0]])]});
            var Q54;
            Q54=makeQuery(id+"F0.imprint","IMPRINT",FACE,{"disambiguationData":[TD([[makeQuery(id+"F0.imprint","IMPRINT",EDGE,{"derivedFrom":sQuery(id+"F0.wireOp",EDGE,"E13.14.0.1")}),1.0]])]});
            var Q55;
            Q55=makeQuery(id+"F0.imprint","IMPRINT",FACE,{"disambiguationData":[TD([[makeQuery(id+"F0.imprint","IMPRINT",EDGE,{"derivedFrom":sQuery(id+"F0.wireOp",EDGE,"E10.14.0.1")}),1.0]])]});
            var Q56;
            Q56=makeQuery(id+"F0.imprint","IMPRINT",FACE,{"disambiguationData":[TD([[makeQuery(id+"F0.imprint","IMPRINT",EDGE,{"derivedFrom":sQuery(id+"F0.wireOp",EDGE,"E10.13.0.1")}),1.0]])]});
            var Q57;
            Q57=makeQuery(id+"F0.imprint","IMPRINT",FACE,{"disambiguationData":[TD([[makeQuery(id+"F0.imprint","IMPRINT",EDGE,{"derivedFrom":sQuery(id+"F0.wireOp",EDGE,"E10.12.0.1")}),1.0]])]});
            var Q58;
            Q58=makeQuery(id+"F0.imprint","IMPRINT",FACE,{"disambiguationData":[TD([[makeQuery(id+"F0.imprint","IMPRINT",EDGE,{"derivedFrom":sQuery(id+"F0.wireOp",EDGE,"E10.11.0.1")}),1.0]])]});
            var Q59;
            Q59=makeQuery(id+"F0.imprint","IMPRINT",FACE,{"disambiguationData":[TD([[makeQuery(id+"F0.imprint","IMPRINT",EDGE,{"derivedFrom":sQuery(id+"F0.wireOp",EDGE,"E16.11.0.0")}),1.0]])]});
            var Q60;
            Q60=makeQuery(id+"F0.imprint","IMPRINT",FACE,{"disambiguationData":[TD([[makeQuery(id+"F0.imprint","IMPRINT",EDGE,{"derivedFrom":sQuery(id+"F0.wireOp",EDGE,"E16.12.0.0")}),1.0]])]});
            var Q61;
            Q61=makeQuery(id+"F0.imprint","IMPRINT",FACE,{"disambiguationData":[TD([[makeQuery(id+"F0.imprint","IMPRINT",EDGE,{"derivedFrom":sQuery(id+"F0.wireOp",EDGE,"E16.13.0.0")}),1.0]])]});
            var Q62;
            Q62=makeQuery(id+"F0.imprint","IMPRINT",FACE,{"disambiguationData":[TD([[makeQuery(id+"F0.imprint","IMPRINT",EDGE,{"derivedFrom":sQuery(id+"F0.wireOp",EDGE,"E16.14.0.0")}),1.0]])]});
            var Q63;
            Q63=makeQuery(id+"F0.imprint","IMPRINT",FACE,{"disambiguationData":[TD([[makeQuery(id+"F0.imprint","IMPRINT",EDGE,{"derivedFrom":sQuery(id+"F0.wireOp",EDGE,"E19.14.0.0")}),1.0]])]});
            var Q64;
            Q64=makeQuery(id+"F0.imprint","IMPRINT",FACE,{"disambiguationData":[TD([[makeQuery(id+"F0.imprint","IMPRINT",EDGE,{"derivedFrom":sQuery(id+"F0.wireOp",EDGE,"E19.13.0.0")}),1.0]])]});
            var Q65;
            Q65=makeQuery(id+"F0.imprint","IMPRINT",FACE,{"disambiguationData":[TD([[makeQuery(id+"F0.imprint","IMPRINT",EDGE,{"derivedFrom":sQuery(id+"F0.wireOp",EDGE,"E19.12.0.0")}),1.0]])]});
            var Q66;
            Q66=makeQuery(id+"F0.imprint","IMPRINT",FACE,{"disambiguationData":[TD([[makeQuery(id+"F0.imprint","IMPRINT",EDGE,{"derivedFrom":sQuery(id+"F0.wireOp",EDGE,"E19.11.0.0")}),1.0]])]});
            var Q67;
            Q67=makeQuery(id+"F0.imprint","IMPRINT",FACE,{"disambiguationData":[TD([[makeQuery(id+"F0.imprint","IMPRINT",EDGE,{"derivedFrom":sQuery(id+"F0.wireOp",EDGE,"E22.11.0.0")}),1.0]])]});
            var Q68;
            Q68=makeQuery(id+"F0.imprint","IMPRINT",FACE,{"disambiguationData":[TD([[makeQuery(id+"F0.imprint","IMPRINT",EDGE,{"derivedFrom":sQuery(id+"F0.wireOp",EDGE,"E22.12.0.0")}),1.0]])]});
            var Q69;
            Q69=makeQuery(id+"F0.imprint","IMPRINT",FACE,{"disambiguationData":[TD([[makeQuery(id+"F0.imprint","IMPRINT",EDGE,{"derivedFrom":sQuery(id+"F0.wireOp",EDGE,"E22.13.0.0")}),1.0]])]});
            var Q70;
            Q70=makeQuery(id+"F0.imprint","IMPRINT",FACE,{"disambiguationData":[TD([[makeQuery(id+"F0.imprint","IMPRINT",EDGE,{"derivedFrom":sQuery(id+"F0.wireOp",EDGE,"E22.14.0.0")}),1.0]])]});
            var Q71;
            Q71=makeQuery(id+"F0.imprint","IMPRINT",FACE,{"disambiguationData":[TD([[makeQuery(id+"F0.imprint","IMPRINT",EDGE,{"derivedFrom":sQuery(id+"F0.wireOp",EDGE,"E27.14.0.0")}),1.0]])]});
            var Q72;
            Q72=makeQuery(id+"F0.imprint","IMPRINT",FACE,{"disambiguationData":[TD([[makeQuery(id+"F0.imprint","IMPRINT",EDGE,{"derivedFrom":sQuery(id+"F0.wireOp",EDGE,"E27.13.0.0")}),1.0]])]});
            var Q73;
            Q73=makeQuery(id+"F0.imprint","IMPRINT",FACE,{"disambiguationData":[TD([[makeQuery(id+"F0.imprint","IMPRINT",EDGE,{"derivedFrom":sQuery(id+"F0.wireOp",EDGE,"E27.12.0.0")}),1.0]])]});
            var Q74;
            Q74=makeQuery(id+"F0.imprint","IMPRINT",FACE,{"disambiguationData":[TD([[makeQuery(id+"F0.imprint","IMPRINT",EDGE,{"derivedFrom":sQuery(id+"F0.wireOp",EDGE,"E27.11.0.0")}),1.0]])]});
            var Q75;
            Q75=makeQuery(id+"F0.imprint","IMPRINT",FACE,{"disambiguationData":[TD([[makeQuery(id+"F0.imprint","IMPRINT",EDGE,{"derivedFrom":sQuery(id+"F0.wireOp",EDGE,"E28.11.0.0")}),1.0]])]});
            var Q76;
            Q76=makeQuery(id+"F0.imprint","IMPRINT",FACE,{"disambiguationData":[TD([[makeQuery(id+"F0.imprint","IMPRINT",EDGE,{"derivedFrom":sQuery(id+"F0.wireOp",EDGE,"E28.12.0.0")}),1.0]])]});
            var Q77;
            Q77=makeQuery(id+"F0.imprint","IMPRINT",FACE,{"disambiguationData":[TD([[makeQuery(id+"F0.imprint","IMPRINT",EDGE,{"derivedFrom":sQuery(id+"F0.wireOp",EDGE,"E28.13.0.0")}),1.0]])]});
            var Q78;
            Q78=makeQuery(id+"F0.imprint","IMPRINT",FACE,{"disambiguationData":[TD([[makeQuery(id+"F0.imprint","IMPRINT",EDGE,{"derivedFrom":sQuery(id+"F0.wireOp",EDGE,"E28.14.0.0")}),1.0]])]});
            var Q79;
            Q79=makeQuery(id+"F0.imprint","IMPRINT",FACE,{"disambiguationData":[TD([[makeQuery(id+"F0.imprint","IMPRINT",EDGE,{"derivedFrom":sQuery(id+"F0.wireOp",EDGE,"E13.9.0.1")}),1.0]])]});
            var Q80;
            Q80=makeQuery(id+"F0.imprint","IMPRINT",FACE,{"disambiguationData":[TD([[makeQuery(id+"F0.imprint","IMPRINT",EDGE,{"derivedFrom":sQuery(id+"F0.wireOp",EDGE,"E13.8.0.1")}),1.0]])]});
            var Q81;
            Q81=makeQuery(id+"F0.imprint","IMPRINT",FACE,{"disambiguationData":[TD([[makeQuery(id+"F0.imprint","IMPRINT",EDGE,{"derivedFrom":sQuery(id+"F0.wireOp",EDGE,"E13.7.0.1")}),1.0]])]});
            var Q82;
            Q82=makeQuery(id+"F0.imprint","IMPRINT",FACE,{"disambiguationData":[TD([[makeQuery(id+"F0.imprint","IMPRINT",EDGE,{"derivedFrom":sQuery(id+"F0.wireOp",EDGE,"E13.6.0.1")}),1.0]])]});
            var Q83;
            Q83=makeQuery(id+"F0.imprint","IMPRINT",FACE,{"disambiguationData":[TD([[makeQuery(id+"F0.imprint","IMPRINT",EDGE,{"derivedFrom":sQuery(id+"F0.wireOp",EDGE,"E13.5.0.1")}),1.0]])]});
            var Q84;
            Q84=makeQuery(id+"F0.imprint","IMPRINT",FACE,{"disambiguationData":[TD([[makeQuery(id+"F0.imprint","IMPRINT",EDGE,{"derivedFrom":sQuery(id+"F0.wireOp",EDGE,"E13.4.0.1")}),1.0]])]});
            var Q85;
            Q85=makeQuery(id+"F0.imprint","IMPRINT",FACE,{"disambiguationData":[TD([[makeQuery(id+"F0.imprint","IMPRINT",EDGE,{"derivedFrom":sQuery(id+"F0.wireOp",EDGE,"E13.3.0.1")}),1.0]])]});
            var Q86;
            Q86=makeQuery(id+"F0.imprint","IMPRINT",FACE,{"disambiguationData":[TD([[makeQuery(id+"F0.imprint","IMPRINT",EDGE,{"derivedFrom":sQuery(id+"F0.wireOp",EDGE,"E13.2.0.1")}),1.0]])]});
            var Q87;
            Q87=makeQuery(id+"F0.imprint","IMPRINT",FACE,{"disambiguationData":[TD([[makeQuery(id+"F0.imprint","IMPRINT",EDGE,{"derivedFrom":sQuery(id+"F0.wireOp",EDGE,"E13.1.0.1")}),1.0]])]});
            var Q88;
            Q88=makeQuery(id+"F0.imprint","IMPRINT",FACE,{"disambiguationData":[TD([[makeQuery(id+"F0.imprint","IMPRINT",EDGE,{"derivedFrom":sQuery(id+"F0.wireOp",EDGE,"E11")}),1.0]])]});
            var Q89;
            Q89=makeQuery(id+"F0.imprint","IMPRINT",FACE,{"disambiguationData":[TD([[makeQuery(id+"F0.imprint","IMPRINT",EDGE,{"derivedFrom":sQuery(id+"F0.wireOp",EDGE,"E8")}),1.0]])]});
            var Q90;
            Q90=makeQuery(id+"F0.imprint","IMPRINT",FACE,{"disambiguationData":[TD([[makeQuery(id+"F0.imprint","IMPRINT",EDGE,{"derivedFrom":sQuery(id+"F0.wireOp",EDGE,"E10.1.0.1")}),1.0]])]});
            var Q91;
            Q91=makeQuery(id+"F0.imprint","IMPRINT",FACE,{"disambiguationData":[TD([[makeQuery(id+"F0.imprint","IMPRINT",EDGE,{"derivedFrom":sQuery(id+"F0.wireOp",EDGE,"E16.1.0.0")}),1.0]])]});
            var Q92;
            Q92=makeQuery(id+"F0.imprint","IMPRINT",FACE,{"disambiguationData":[TD([[makeQuery(id+"F0.imprint","IMPRINT",EDGE,{"derivedFrom":sQuery(id+"F0.wireOp",EDGE,"E14")}),1.0]])]});
            var Q93;
            Q93=makeQuery(id+"F0.imprint","IMPRINT",FACE,{"disambiguationData":[TD([[makeQuery(id+"F0.imprint","IMPRINT",EDGE,{"derivedFrom":sQuery(id+"F0.wireOp",EDGE,"E17")}),1.0]])]});
            var Q94;
            Q94=makeQuery(id+"F0.imprint","IMPRINT",FACE,{"disambiguationData":[TD([[makeQuery(id+"F0.imprint","IMPRINT",EDGE,{"derivedFrom":sQuery(id+"F0.wireOp",EDGE,"E19.1.0.0")}),1.0]])]});
            var Q95;
            Q95=makeQuery(id+"F0.imprint","IMPRINT",FACE,{"disambiguationData":[TD([[makeQuery(id+"F0.imprint","IMPRINT",EDGE,{"derivedFrom":sQuery(id+"F0.wireOp",EDGE,"E19.2.0.0")}),1.0]])]});
            var Q96;
            Q96=makeQuery(id+"F0.imprint","IMPRINT",FACE,{"disambiguationData":[TD([[makeQuery(id+"F0.imprint","IMPRINT",EDGE,{"derivedFrom":sQuery(id+"F0.wireOp",EDGE,"E19.3.0.0")}),1.0]])]});
            var Q97;
            Q97=makeQuery(id+"F0.imprint","IMPRINT",FACE,{"disambiguationData":[TD([[makeQuery(id+"F0.imprint","IMPRINT",EDGE,{"derivedFrom":sQuery(id+"F0.wireOp",EDGE,"E16.3.0.0")}),1.0]])]});
            var Q98;
            Q98=makeQuery(id+"F0.imprint","IMPRINT",FACE,{"disambiguationData":[TD([[makeQuery(id+"F0.imprint","IMPRINT",EDGE,{"derivedFrom":sQuery(id+"F0.wireOp",EDGE,"E22.2.0.0")}),1.0]])]});
            var Q99;
            Q99=makeQuery(id+"F0.imprint","IMPRINT",FACE,{"disambiguationData":[TD([[makeQuery(id+"F0.imprint","IMPRINT",EDGE,{"derivedFrom":sQuery(id+"F0.wireOp",EDGE,"E22.1.0.0")}),1.0]])]});
            var Q100;
            Q100=makeQuery(id+"F0.imprint","IMPRINT",FACE,{"disambiguationData":[TD([[makeQuery(id+"F0.imprint","IMPRINT",EDGE,{"derivedFrom":sQuery(id+"F0.wireOp",EDGE,"E20")}),1.0]])]});
            var Q101;
            Q101=makeQuery(id+"F0.imprint","IMPRINT",FACE,{"disambiguationData":[TD([[makeQuery(id+"F0.imprint","IMPRINT",EDGE,{"derivedFrom":sQuery(id+"F0.wireOp",EDGE,"E23")}),1.0]])]});
            var Q102;
            Q102=makeQuery(id+"F0.imprint","IMPRINT",FACE,{"disambiguationData":[TD([[makeQuery(id+"F0.imprint","IMPRINT",EDGE,{"derivedFrom":sQuery(id+"F0.wireOp",EDGE,"E27.1.0.0")}),1.0]])]});
            var Q103;
            Q103=makeQuery(id+"F0.imprint","IMPRINT",FACE,{"disambiguationData":[TD([[makeQuery(id+"F0.imprint","IMPRINT",EDGE,{"derivedFrom":sQuery(id+"F0.wireOp",EDGE,"E28.1.0.0")}),1.0]])]});
            var Q104;
            Q104=makeQuery(id+"F0.imprint","IMPRINT",FACE,{"disambiguationData":[TD([[makeQuery(id+"F0.imprint","IMPRINT",EDGE,{"derivedFrom":sQuery(id+"F0.wireOp",EDGE,"E25")}),1.0]])]});
            extrude(context, id + "F4", {"entities" : qUnion([Q0, Q1, Q2, Q3, Q4, Q5, Q6, Q7, Q8, Q9, Q10, Q11, Q12, Q13, Q14, Q15, Q16, Q17, Q18, Q19, Q20, Q21, Q22, Q23, Q24, Q25, Q26, Q27, Q28, Q29, Q30, Q31, Q32, Q33, Q34, Q35, Q36, Q37, Q38, Q39, Q40, Q41, Q42, Q43, Q44, Q45, Q46, Q47, Q48, Q49, Q50, Q51, Q52, Q53, Q54, Q55, Q56, Q57, Q58, Q59, Q60, Q61, Q62, Q63, Q64, Q65, Q66, Q67, Q68, Q69, Q70, Q71, Q72, Q73, Q74, Q75, Q76, Q77, Q78, Q79, Q80, Q81, Q82, Q83, Q84, Q85, Q86, Q87, Q88, Q89, Q90, Q91, Q92, Q93, Q94, Q95, Q96, Q97, Q98, Q99, Q100, Q101, Q102, Q103, Q104]), "operationType" : NewBodyOperationType.ADD, "depth" : .8 * mm, "offsetDistance" : 25.4 * mm});
        }
    });
